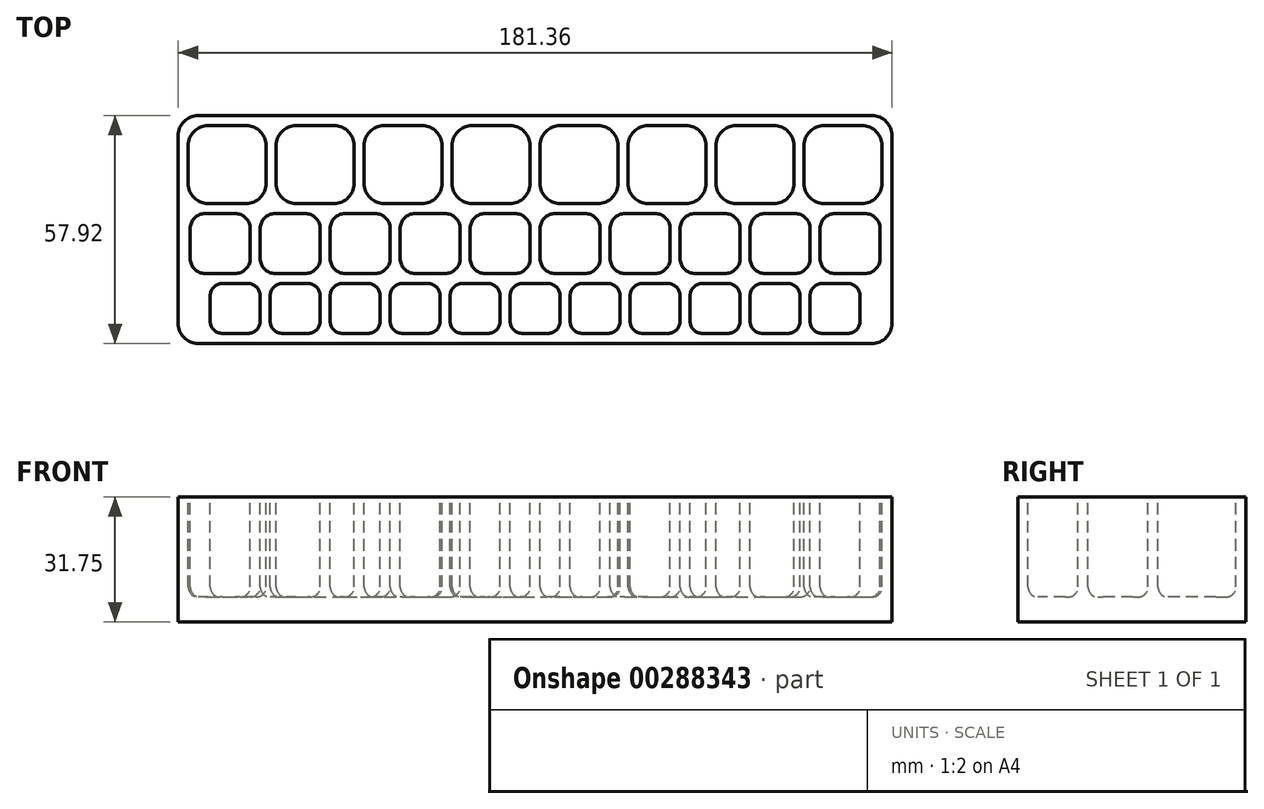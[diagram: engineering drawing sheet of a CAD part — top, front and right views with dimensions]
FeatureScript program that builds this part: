
annotation { "Feature Type Name" : "Feature", "Feature Type Description" : "" }
export const myFeature = defineFeature(function(context is Context, id is Id, definition is map)
    precondition{}
    {
        {
            var Q0;
            Q0=qCreatedBy(makeId("Top.planeOp"),FACE);
            var sketch = newSketch(context, id + "F0", { "sketchPlane" : qUnion([Q0])});
            skLineSegment(sketch, "E0.bottom", {"start": v(-90.68, 28.96) * mm, "end": v(90.68, 28.96) * mm});
            skLineSegment(sketch, "E0.top", {"start": v(-90.68, -28.96) * mm, "end": v(90.68, -28.96) * mm});
            skLineSegment(sketch, "E0.left", {"start": v(-90.68, 28.96) * mm, "end": v(-90.68, -28.96) * mm});
            skLineSegment(sketch, "E0.right", {"start": v(90.68, 28.96) * mm, "end": v(90.68, -28.96) * mm});
            skLineSegment(sketch, "E1.bottom", {"start": v(-88.14, 26.42) * mm, "end": v(-68.33, 26.42) * mm});
            skLineSegment(sketch, "E1.top", {"start": v(-88.14, 6.6) * mm, "end": v(-68.33, 6.6) * mm});
            skLineSegment(sketch, "E1.left", {"start": v(-88.14, 26.42) * mm, "end": v(-88.14, 6.6) * mm});
            skLineSegment(sketch, "E1.right", {"start": v(-68.33, 26.42) * mm, "end": v(-68.33, 6.6) * mm});
            skLineSegment(sketch, "E2.1.0.0", {"start": v(-65.79, 6.6) * mm, "end": v(-45.97, 6.6) * mm});
            skLineSegment(sketch, "E2.1.0.1", {"start": v(-45.97, 26.42) * mm, "end": v(-45.97, 6.6) * mm});
            skLineSegment(sketch, "E2.1.0.2", {"start": v(-65.79, 26.42) * mm, "end": v(-45.97, 26.42) * mm});
            skLineSegment(sketch, "E2.1.0.3", {"start": v(-65.79, 26.42) * mm, "end": v(-65.79, 6.6) * mm});
            skLineSegment(sketch, "E2.2.0.0", {"start": v(-43.43, 6.6) * mm, "end": v(-23.62, 6.6) * mm});
            skLineSegment(sketch, "E2.2.0.1", {"start": v(-23.62, 26.42) * mm, "end": v(-23.62, 6.6) * mm});
            skLineSegment(sketch, "E2.2.0.2", {"start": v(-43.43, 26.42) * mm, "end": v(-23.62, 26.42) * mm});
            skLineSegment(sketch, "E2.2.0.3", {"start": v(-43.43, 26.42) * mm, "end": v(-43.43, 6.6) * mm});
            skLineSegment(sketch, "E2.direction1", {"start": v(-88.14, 6.6) * mm, "end": v(-65.79, 6.6) * mm, "construction": true});
            skLineSegment(sketch, "E3.0.3.0", {"start": v(-21.08, 6.6) * mm, "end": v(-1.27, 6.6) * mm});
            skLineSegment(sketch, "E3.3.3.0", {"start": v(-1.27, 26.42) * mm, "end": v(-1.27, 6.6) * mm});
            skLineSegment(sketch, "E3.6.3.0", {"start": v(-21.08, 26.42) * mm, "end": v(-1.27, 26.42) * mm});
            skLineSegment(sketch, "E3.9.3.0", {"start": v(-21.08, 26.42) * mm, "end": v(-21.08, 6.6) * mm});
            skLineSegment(sketch, "E3.0.4.0", {"start": v(1.27, 6.6) * mm, "end": v(21.08, 6.6) * mm});
            skLineSegment(sketch, "E3.3.4.0", {"start": v(21.08, 26.42) * mm, "end": v(21.08, 6.6) * mm});
            skLineSegment(sketch, "E3.6.4.0", {"start": v(1.27, 26.42) * mm, "end": v(21.08, 26.42) * mm});
            skLineSegment(sketch, "E3.9.4.0", {"start": v(1.27, 26.42) * mm, "end": v(1.27, 6.6) * mm});
            skLineSegment(sketch, "E3.0.5.0", {"start": v(23.62, 6.6) * mm, "end": v(43.43, 6.6) * mm});
            skLineSegment(sketch, "E3.3.5.0", {"start": v(43.43, 26.42) * mm, "end": v(43.43, 6.6) * mm});
            skLineSegment(sketch, "E3.6.5.0", {"start": v(23.62, 26.42) * mm, "end": v(43.43, 26.42) * mm});
            skLineSegment(sketch, "E3.9.5.0", {"start": v(23.62, 26.42) * mm, "end": v(23.62, 6.6) * mm});
            skLineSegment(sketch, "E3.0.6.0", {"start": v(45.97, 6.6) * mm, "end": v(65.79, 6.6) * mm});
            skLineSegment(sketch, "E3.3.6.0", {"start": v(65.79, 26.42) * mm, "end": v(65.79, 6.6) * mm});
            skLineSegment(sketch, "E3.6.6.0", {"start": v(45.97, 26.42) * mm, "end": v(65.79, 26.42) * mm});
            skLineSegment(sketch, "E3.9.6.0", {"start": v(45.97, 26.42) * mm, "end": v(45.97, 6.6) * mm});
            skLineSegment(sketch, "E3.0.7.0", {"start": v(68.33, 6.6) * mm, "end": v(88.14, 6.6) * mm});
            skLineSegment(sketch, "E3.3.7.0", {"start": v(88.14, 26.42) * mm, "end": v(88.14, 6.6) * mm});
            skLineSegment(sketch, "E3.6.7.0", {"start": v(68.33, 26.42) * mm, "end": v(88.14, 26.42) * mm});
            skLineSegment(sketch, "E3.9.7.0", {"start": v(68.33, 26.42) * mm, "end": v(68.33, 6.6) * mm});
            skLineSegment(sketch, "E4.bottom", {"start": v(-87.63, 4.06) * mm, "end": v(-72.4, 4.06) * mm});
            skLineSegment(sketch, "E4.top", {"start": v(-87.63, -11.18) * mm, "end": v(-72.4, -11.18) * mm});
            skLineSegment(sketch, "E4.left", {"start": v(-87.63, 4.06) * mm, "end": v(-87.63, -11.18) * mm});
            skLineSegment(sketch, "E4.right", {"start": v(-72.4, 4.06) * mm, "end": v(-72.4, -11.18) * mm});
            skLineSegment(sketch, "E5.1.0.0", {"start": v(-54.61, 4.06) * mm, "end": v(-54.61, -11.18) * mm});
            skLineSegment(sketch, "E5.1.0.1", {"start": v(-69.85, 4.06) * mm, "end": v(-54.61, 4.06) * mm});
            skLineSegment(sketch, "E5.1.0.2", {"start": v(-69.85, 4.06) * mm, "end": v(-69.85, -11.18) * mm});
            skLineSegment(sketch, "E5.1.0.3", {"start": v(-69.85, -11.18) * mm, "end": v(-54.61, -11.18) * mm});
            skLineSegment(sketch, "E5.2.0.0", {"start": v(-36.83, 4.06) * mm, "end": v(-36.83, -11.18) * mm});
            skLineSegment(sketch, "E5.2.0.1", {"start": v(-52.07, 4.06) * mm, "end": v(-36.83, 4.06) * mm});
            skLineSegment(sketch, "E5.2.0.2", {"start": v(-52.07, 4.06) * mm, "end": v(-52.07, -11.18) * mm});
            skLineSegment(sketch, "E5.2.0.3", {"start": v(-52.07, -11.18) * mm, "end": v(-36.83, -11.18) * mm});
            skLineSegment(sketch, "E5.3.0.0", {"start": v(-19.05, 4.06) * mm, "end": v(-19.05, -11.18) * mm});
            skLineSegment(sketch, "E5.3.0.1", {"start": v(-34.3, 4.06) * mm, "end": v(-19.05, 4.06) * mm});
            skLineSegment(sketch, "E5.3.0.2", {"start": v(-34.29, 4.06) * mm, "end": v(-34.29, -11.18) * mm});
            skLineSegment(sketch, "E5.3.0.3", {"start": v(-34.3, -11.18) * mm, "end": v(-19.05, -11.18) * mm});
            skLineSegment(sketch, "E5.4.0.0", {"start": v(-1.27, 4.06) * mm, "end": v(-1.27, -11.18) * mm});
            skLineSegment(sketch, "E5.4.0.1", {"start": v(-16.5, 4.06) * mm, "end": v(-1.27, 4.06) * mm});
            skLineSegment(sketch, "E5.4.0.2", {"start": v(-16.5, 4.06) * mm, "end": v(-16.5, -11.18) * mm});
            skLineSegment(sketch, "E5.4.0.3", {"start": v(-16.5, -11.18) * mm, "end": v(-1.27, -11.18) * mm});
            skLineSegment(sketch, "E5.5.0.0", {"start": v(16.51, 4.06) * mm, "end": v(16.51, -11.18) * mm});
            skLineSegment(sketch, "E5.5.0.1", {"start": v(1.27, 4.06) * mm, "end": v(16.51, 4.06) * mm});
            skLineSegment(sketch, "E5.5.0.2", {"start": v(1.27, 4.06) * mm, "end": v(1.27, -11.18) * mm});
            skLineSegment(sketch, "E5.5.0.3", {"start": v(1.27, -11.18) * mm, "end": v(16.51, -11.18) * mm});
            skLineSegment(sketch, "E5.6.0.0", {"start": v(34.3, 4.06) * mm, "end": v(34.3, -11.18) * mm});
            skLineSegment(sketch, "E5.6.0.1", {"start": v(19.05, 4.06) * mm, "end": v(34.3, 4.06) * mm});
            skLineSegment(sketch, "E5.6.0.2", {"start": v(19.05, 4.06) * mm, "end": v(19.05, -11.18) * mm});
            skLineSegment(sketch, "E5.6.0.3", {"start": v(19.05, -11.18) * mm, "end": v(34.3, -11.18) * mm});
            skLineSegment(sketch, "E5.7.0.0", {"start": v(52.07, 4.06) * mm, "end": v(52.07, -11.18) * mm});
            skLineSegment(sketch, "E5.7.0.1", {"start": v(36.83, 4.06) * mm, "end": v(52.07, 4.06) * mm});
            skLineSegment(sketch, "E5.7.0.2", {"start": v(36.83, 4.06) * mm, "end": v(36.83, -11.18) * mm});
            skLineSegment(sketch, "E5.7.0.3", {"start": v(36.83, -11.18) * mm, "end": v(52.07, -11.18) * mm});
            skLineSegment(sketch, "E5.direction1", {"start": v(-72.4, -11.18) * mm, "end": v(-54.61, -11.18) * mm, "construction": true});
            skLineSegment(sketch, "E6.bottom", {"start": v(-82.55, -13.72) * mm, "end": v(-69.85, -13.72) * mm});
            skLineSegment(sketch, "E6.top", {"start": v(-82.55, -26.42) * mm, "end": v(-69.85, -26.42) * mm});
            skLineSegment(sketch, "E6.left", {"start": v(-82.55, -13.72) * mm, "end": v(-82.55, -26.42) * mm});
            skLineSegment(sketch, "E6.right", {"start": v(-69.85, -13.72) * mm, "end": v(-69.85, -26.42) * mm});
            skLineSegment(sketch, "E7.1.0.0", {"start": v(-67.31, -13.72) * mm, "end": v(-54.61, -13.72) * mm});
            skLineSegment(sketch, "E7.1.0.1", {"start": v(-67.31, -13.72) * mm, "end": v(-67.31, -26.42) * mm});
            skLineSegment(sketch, "E7.1.0.2", {"start": v(-67.31, -26.42) * mm, "end": v(-54.61, -26.42) * mm});
            skLineSegment(sketch, "E7.1.0.3", {"start": v(-54.61, -13.72) * mm, "end": v(-54.61, -26.42) * mm});
            skLineSegment(sketch, "E7.2.0.0", {"start": v(-52.07, -13.72) * mm, "end": v(-39.37, -13.72) * mm});
            skLineSegment(sketch, "E7.2.0.1", {"start": v(-52.07, -13.72) * mm, "end": v(-52.07, -26.42) * mm});
            skLineSegment(sketch, "E7.2.0.2", {"start": v(-52.07, -26.42) * mm, "end": v(-39.37, -26.42) * mm});
            skLineSegment(sketch, "E7.2.0.3", {"start": v(-39.37, -13.72) * mm, "end": v(-39.37, -26.42) * mm});
            skLineSegment(sketch, "E7.3.0.0", {"start": v(-36.83, -13.72) * mm, "end": v(-24.13, -13.72) * mm});
            skLineSegment(sketch, "E7.3.0.1", {"start": v(-36.83, -13.72) * mm, "end": v(-36.83, -26.42) * mm});
            skLineSegment(sketch, "E7.3.0.2", {"start": v(-36.83, -26.42) * mm, "end": v(-24.13, -26.42) * mm});
            skLineSegment(sketch, "E7.3.0.3", {"start": v(-24.13, -13.72) * mm, "end": v(-24.13, -26.42) * mm});
            skLineSegment(sketch, "E7.4.0.0", {"start": v(-21.59, -13.72) * mm, "end": v(-8.89, -13.72) * mm});
            skLineSegment(sketch, "E7.4.0.1", {"start": v(-21.59, -13.72) * mm, "end": v(-21.59, -26.42) * mm});
            skLineSegment(sketch, "E7.4.0.2", {"start": v(-21.59, -26.42) * mm, "end": v(-8.89, -26.42) * mm});
            skLineSegment(sketch, "E7.4.0.3", {"start": v(-8.89, -13.72) * mm, "end": v(-8.89, -26.42) * mm});
            skLineSegment(sketch, "E7.5.0.0", {"start": v(-6.35, -13.72) * mm, "end": v(6.35, -13.72) * mm});
            skLineSegment(sketch, "E7.5.0.1", {"start": v(-6.35, -13.72) * mm, "end": v(-6.35, -26.42) * mm});
            skLineSegment(sketch, "E7.5.0.2", {"start": v(-6.35, -26.42) * mm, "end": v(6.35, -26.42) * mm});
            skLineSegment(sketch, "E7.5.0.3", {"start": v(6.35, -13.72) * mm, "end": v(6.35, -26.42) * mm});
            skLineSegment(sketch, "E7.6.0.0", {"start": v(8.9, -13.72) * mm, "end": v(21.6, -13.72) * mm});
            skLineSegment(sketch, "E7.6.0.1", {"start": v(8.9, -13.72) * mm, "end": v(8.9, -26.42) * mm});
            skLineSegment(sketch, "E7.6.0.2", {"start": v(8.9, -26.42) * mm, "end": v(21.6, -26.42) * mm});
            skLineSegment(sketch, "E7.6.0.3", {"start": v(21.6, -13.72) * mm, "end": v(21.6, -26.42) * mm});
            skLineSegment(sketch, "E7.7.0.0", {"start": v(24.13, -13.72) * mm, "end": v(36.83, -13.72) * mm});
            skLineSegment(sketch, "E7.7.0.1", {"start": v(24.13, -13.72) * mm, "end": v(24.13, -26.42) * mm});
            skLineSegment(sketch, "E7.7.0.2", {"start": v(24.13, -26.42) * mm, "end": v(36.83, -26.42) * mm});
            skLineSegment(sketch, "E7.7.0.3", {"start": v(36.83, -13.72) * mm, "end": v(36.83, -26.42) * mm});
            skLineSegment(sketch, "E7.direction1", {"start": v(-82.55, -26.42) * mm, "end": v(-67.31, -26.42) * mm, "construction": true});
            skLineSegment(sketch, "E8", {"start": v(-88.14, 26.42) * mm, "end": v(-88.14, 28.96) * mm, "construction": true});
            skLineSegment(sketch, "E9.0.8.0", {"start": v(69.85, 4.06) * mm, "end": v(69.85, -11.18) * mm});
            skLineSegment(sketch, "E9.3.8.0", {"start": v(54.61, 4.06) * mm, "end": v(69.85, 4.06) * mm});
            skLineSegment(sketch, "E9.6.8.0", {"start": v(54.61, 4.06) * mm, "end": v(54.61, -11.18) * mm});
            skLineSegment(sketch, "E9.9.8.0", {"start": v(54.61, -11.18) * mm, "end": v(69.85, -11.18) * mm});
            skLineSegment(sketch, "E9.0.9.0", {"start": v(87.63, 4.06) * mm, "end": v(87.63, -11.18) * mm});
            skLineSegment(sketch, "E9.3.9.0", {"start": v(72.4, 4.06) * mm, "end": v(87.63, 4.06) * mm});
            skLineSegment(sketch, "E9.6.9.0", {"start": v(72.4, 4.06) * mm, "end": v(72.4, -11.18) * mm});
            skLineSegment(sketch, "E9.9.9.0", {"start": v(72.4, -11.18) * mm, "end": v(87.63, -11.18) * mm});
            skLineSegment(sketch, "E10.0.8.0", {"start": v(39.37, -13.72) * mm, "end": v(52.07, -13.72) * mm});
            skLineSegment(sketch, "E10.3.8.0", {"start": v(39.37, -13.72) * mm, "end": v(39.37, -26.42) * mm});
            skLineSegment(sketch, "E10.6.8.0", {"start": v(39.37, -26.42) * mm, "end": v(52.07, -26.42) * mm});
            skLineSegment(sketch, "E10.9.8.0", {"start": v(52.07, -13.72) * mm, "end": v(52.07, -26.42) * mm});
            skLineSegment(sketch, "E10.0.9.0", {"start": v(54.61, -13.72) * mm, "end": v(67.31, -13.72) * mm});
            skLineSegment(sketch, "E10.3.9.0", {"start": v(54.61, -13.72) * mm, "end": v(54.61, -26.42) * mm});
            skLineSegment(sketch, "E10.6.9.0", {"start": v(54.61, -26.42) * mm, "end": v(67.31, -26.42) * mm});
            skLineSegment(sketch, "E10.9.9.0", {"start": v(67.31, -13.72) * mm, "end": v(67.31, -26.42) * mm});
            skLineSegment(sketch, "E10.0.10.0", {"start": v(69.85, -13.72) * mm, "end": v(82.55, -13.72) * mm});
            skLineSegment(sketch, "E10.3.10.0", {"start": v(69.85, -13.72) * mm, "end": v(69.85, -26.42) * mm});
            skLineSegment(sketch, "E10.6.10.0", {"start": v(69.85, -26.42) * mm, "end": v(82.55, -26.42) * mm});
            skLineSegment(sketch, "E10.9.10.0", {"start": v(82.55, -13.72) * mm, "end": v(82.55, -26.42) * mm});
            skLineSegment(sketch, "E11", {"start": v(82.55, -20.07) * mm, "end": v(90.68, -20.07) * mm, "construction": true});
            skLineSegment(sketch, "E12", {"start": v(-87.63, -3.56) * mm, "end": v(-90.68, -3.56) * mm, "construction": true});
            skLineSegment(sketch, "E13", {"start": v(87.63, -3.56) * mm, "end": v(90.68, -3.56) * mm, "construction": true});
            skLineSegment(sketch, "E14", {"start": v(88.14, 16.5) * mm, "end": v(90.68, 16.5) * mm, "construction": true});
            skLineSegment(sketch, "E15", {"start": v(-88.14, 16.5) * mm, "end": v(-90.68, 16.5) * mm, "construction": true});
            skLineSegment(sketch, "E16", {"start": v(-76.2, -26.42) * mm, "end": v(-76.2, -28.96) * mm, "construction": true});
            skLineSegment(sketch, "E17", {"start": v(-80.01, -11.18) * mm, "end": v(-80.01, -13.72) * mm, "construction": true});
            skLineSegment(sketch, "E18", {"start": v(-78.23, 6.6) * mm, "end": v(-78.23, 4.06) * mm, "construction": true});
            skLineSegment(sketch, "E19", {"start": v(-78.23, 26.42) * mm, "end": v(-78.23, 28.96) * mm, "construction": true});
            skLineSegment(sketch, "E20", {"start": v(-82.55, -20.07) * mm, "end": v(-90.68, -20.07) * mm, "construction": true});
            skLineSegment(sketch, "E21", {"start": v(-90.68, 0) * mm, "end": v(0, 0) * mm, "construction": true});
            skLineSegment(sketch, "E22", {"start": v(0, 0) * mm, "end": v(90.68, 0) * mm, "construction": true});
            skSolve(sketch);
        }
        {
            var Q0;
            Q0 = qSketchRegion(id + "F0", true);
            var Q1;
            Q1=makeQuery(id+"F0.imprint","IMPRINT",FACE,{"disambiguationData":[TD([[makeQuery(id+"F0.imprint","IMPRINT",EDGE,{"derivedFrom":sQuery(id+"F0.wireOp",EDGE,"E1.bottom")}),-1.0]])]});
            var Q2;
            Q2=makeQuery(id+"F0.imprint","IMPRINT",FACE,{"disambiguationData":[TD([[makeQuery(id+"F0.imprint","IMPRINT",EDGE,{"derivedFrom":sQuery(id+"F0.wireOp",EDGE,"E2.1.0.0")}),1.0]])]});
            var Q3;
            Q3=makeQuery(id+"F0.imprint","IMPRINT",FACE,{"disambiguationData":[TD([[makeQuery(id+"F0.imprint","IMPRINT",EDGE,{"derivedFrom":sQuery(id+"F0.wireOp",EDGE,"E2.2.0.0")}),1.0]])]});
            var Q4;
            Q4=makeQuery(id+"F0.imprint","IMPRINT",FACE,{"disambiguationData":[TD([[makeQuery(id+"F0.imprint","IMPRINT",EDGE,{"derivedFrom":sQuery(id+"F0.wireOp",EDGE,"E3.0.3.0")}),1.0]])]});
            var Q5;
            Q5=makeQuery(id+"F0.imprint","IMPRINT",FACE,{"disambiguationData":[TD([[makeQuery(id+"F0.imprint","IMPRINT",EDGE,{"derivedFrom":sQuery(id+"F0.wireOp",EDGE,"E3.0.4.0")}),1.0]])]});
            var Q6;
            Q6=makeQuery(id+"F0.imprint","IMPRINT",FACE,{"disambiguationData":[TD([[makeQuery(id+"F0.imprint","IMPRINT",EDGE,{"derivedFrom":sQuery(id+"F0.wireOp",EDGE,"E3.0.5.0")}),1.0]])]});
            var Q7;
            Q7=makeQuery(id+"F0.imprint","IMPRINT",FACE,{"disambiguationData":[TD([[makeQuery(id+"F0.imprint","IMPRINT",EDGE,{"derivedFrom":sQuery(id+"F0.wireOp",EDGE,"E3.0.6.0")}),1.0]])]});
            var Q8;
            Q8=makeQuery(id+"F0.imprint","IMPRINT",FACE,{"disambiguationData":[TD([[makeQuery(id+"F0.imprint","IMPRINT",EDGE,{"derivedFrom":sQuery(id+"F0.wireOp",EDGE,"E3.0.7.0")}),1.0]])]});
            var Q9;
            Q9=makeQuery(id+"F0.imprint","IMPRINT",FACE,{"disambiguationData":[TD([[makeQuery(id+"F0.imprint","IMPRINT",EDGE,{"derivedFrom":sQuery(id+"F0.wireOp",EDGE,"E4.bottom")}),-1.0]])]});
            var Q10;
            Q10=makeQuery(id+"F0.imprint","IMPRINT",FACE,{"disambiguationData":[TD([[makeQuery(id+"F0.imprint","IMPRINT",EDGE,{"derivedFrom":sQuery(id+"F0.wireOp",EDGE,"E5.1.0.0")}),-1.0]])]});
            var Q11;
            Q11=makeQuery(id+"F0.imprint","IMPRINT",FACE,{"disambiguationData":[TD([[makeQuery(id+"F0.imprint","IMPRINT",EDGE,{"derivedFrom":sQuery(id+"F0.wireOp",EDGE,"E5.2.0.0")}),-1.0]])]});
            var Q12;
            Q12=makeQuery(id+"F0.imprint","IMPRINT",FACE,{"disambiguationData":[TD([[makeQuery(id+"F0.imprint","IMPRINT",EDGE,{"derivedFrom":sQuery(id+"F0.wireOp",EDGE,"E5.3.0.0")}),-1.0]])]});
            var Q13;
            Q13=makeQuery(id+"F0.imprint","IMPRINT",FACE,{"disambiguationData":[TD([[makeQuery(id+"F0.imprint","IMPRINT",EDGE,{"derivedFrom":sQuery(id+"F0.wireOp",EDGE,"E5.4.0.0")}),-1.0]])]});
            var Q14;
            Q14=makeQuery(id+"F0.imprint","IMPRINT",FACE,{"disambiguationData":[TD([[makeQuery(id+"F0.imprint","IMPRINT",EDGE,{"derivedFrom":sQuery(id+"F0.wireOp",EDGE,"E5.5.0.0")}),-1.0]])]});
            var Q15;
            Q15=makeQuery(id+"F0.imprint","IMPRINT",FACE,{"disambiguationData":[TD([[makeQuery(id+"F0.imprint","IMPRINT",EDGE,{"derivedFrom":sQuery(id+"F0.wireOp",EDGE,"E5.6.0.0")}),-1.0]])]});
            var Q16;
            Q16=makeQuery(id+"F0.imprint","IMPRINT",FACE,{"disambiguationData":[TD([[makeQuery(id+"F0.imprint","IMPRINT",EDGE,{"derivedFrom":sQuery(id+"F0.wireOp",EDGE,"E5.7.0.0")}),-1.0]])]});
            var Q17;
            Q17=makeQuery(id+"F0.imprint","IMPRINT",FACE,{"disambiguationData":[TD([[makeQuery(id+"F0.imprint","IMPRINT",EDGE,{"derivedFrom":sQuery(id+"F0.wireOp",EDGE,"E9.0.8.0")}),-1.0]])]});
            var Q18;
            Q18=makeQuery(id+"F0.imprint","IMPRINT",FACE,{"disambiguationData":[TD([[makeQuery(id+"F0.imprint","IMPRINT",EDGE,{"derivedFrom":sQuery(id+"F0.wireOp",EDGE,"E9.0.9.0")}),-1.0]])]});
            var Q19;
            Q19=makeQuery(id+"F0.imprint","IMPRINT",FACE,{"disambiguationData":[TD([[makeQuery(id+"F0.imprint","IMPRINT",EDGE,{"derivedFrom":sQuery(id+"F0.wireOp",EDGE,"E6.bottom")}),-1.0]])]});
            var Q20;
            Q20=makeQuery(id+"F0.imprint","IMPRINT",FACE,{"disambiguationData":[TD([[makeQuery(id+"F0.imprint","IMPRINT",EDGE,{"derivedFrom":sQuery(id+"F0.wireOp",EDGE,"E7.1.0.0")}),-1.0]])]});
            var Q21;
            Q21=makeQuery(id+"F0.imprint","IMPRINT",FACE,{"disambiguationData":[TD([[makeQuery(id+"F0.imprint","IMPRINT",EDGE,{"derivedFrom":sQuery(id+"F0.wireOp",EDGE,"E7.2.0.0")}),-1.0]])]});
            var Q22;
            Q22=makeQuery(id+"F0.imprint","IMPRINT",FACE,{"disambiguationData":[TD([[makeQuery(id+"F0.imprint","IMPRINT",EDGE,{"derivedFrom":sQuery(id+"F0.wireOp",EDGE,"E7.3.0.0")}),-1.0]])]});
            var Q23;
            Q23=makeQuery(id+"F0.imprint","IMPRINT",FACE,{"disambiguationData":[TD([[makeQuery(id+"F0.imprint","IMPRINT",EDGE,{"derivedFrom":sQuery(id+"F0.wireOp",EDGE,"E7.4.0.0")}),-1.0]])]});
            var Q24;
            Q24=makeQuery(id+"F0.imprint","IMPRINT",FACE,{"disambiguationData":[TD([[makeQuery(id+"F0.imprint","IMPRINT",EDGE,{"derivedFrom":sQuery(id+"F0.wireOp",EDGE,"E7.5.0.0")}),-1.0]])]});
            var Q25;
            Q25=makeQuery(id+"F0.imprint","IMPRINT",FACE,{"disambiguationData":[TD([[makeQuery(id+"F0.imprint","IMPRINT",EDGE,{"derivedFrom":sQuery(id+"F0.wireOp",EDGE,"E7.6.0.0")}),-1.0]])]});
            var Q26;
            Q26=makeQuery(id+"F0.imprint","IMPRINT",FACE,{"disambiguationData":[TD([[makeQuery(id+"F0.imprint","IMPRINT",EDGE,{"derivedFrom":sQuery(id+"F0.wireOp",EDGE,"E7.7.0.0")}),-1.0]])]});
            var Q27;
            Q27=makeQuery(id+"F0.imprint","IMPRINT",FACE,{"disambiguationData":[TD([[makeQuery(id+"F0.imprint","IMPRINT",EDGE,{"derivedFrom":sQuery(id+"F0.wireOp",EDGE,"E10.0.8.0")}),-1.0]])]});
            var Q28;
            Q28=makeQuery(id+"F0.imprint","IMPRINT",FACE,{"disambiguationData":[TD([[makeQuery(id+"F0.imprint","IMPRINT",EDGE,{"derivedFrom":sQuery(id+"F0.wireOp",EDGE,"E10.0.9.0")}),-1.0]])]});
            var Q29;
            Q29=makeQuery(id+"F0.imprint","IMPRINT",FACE,{"disambiguationData":[TD([[makeQuery(id+"F0.imprint","IMPRINT",EDGE,{"derivedFrom":sQuery(id+"F0.wireOp",EDGE,"E10.0.10.0")}),-1.0]])]});
            extrude(context, id + "F1", {"entities" : qUnion([Q0, Q1, Q2, Q3, Q4, Q5, Q6, Q7, Q8, Q9, Q10, Q11, Q12, Q13, Q14, Q15, Q16, Q17, Q18, Q19, Q20, Q21, Q22, Q23, Q24, Q25, Q26, Q27, Q28, Q29]), "oppositeDirection" : true, "depth" : 31.75 * mm});
        }
        {
            var Q0;
            Q0=makeQuery(id+"F0.imprint","IMPRINT",FACE,{"disambiguationData":[TD([[makeQuery(id+"F0.imprint","IMPRINT",EDGE,{"derivedFrom":sQuery(id+"F0.wireOp",EDGE,"E6.bottom")}),-1.0]])]});
            var Q1;
            Q1=makeQuery(id+"F0.imprint","IMPRINT",FACE,{"disambiguationData":[TD([[makeQuery(id+"F0.imprint","IMPRINT",EDGE,{"derivedFrom":sQuery(id+"F0.wireOp",EDGE,"E7.1.0.0")}),-1.0]])]});
            var Q2;
            Q2=makeQuery(id+"F0.imprint","IMPRINT",FACE,{"disambiguationData":[TD([[makeQuery(id+"F0.imprint","IMPRINT",EDGE,{"derivedFrom":sQuery(id+"F0.wireOp",EDGE,"E4.bottom")}),-1.0]])]});
            var Q3;
            Q3=makeQuery(id+"F0.imprint","IMPRINT",FACE,{"disambiguationData":[TD([[makeQuery(id+"F0.imprint","IMPRINT",EDGE,{"derivedFrom":sQuery(id+"F0.wireOp",EDGE,"E5.1.0.0")}),-1.0]])]});
            var Q4;
            Q4=makeQuery(id+"F0.imprint","IMPRINT",FACE,{"disambiguationData":[TD([[makeQuery(id+"F0.imprint","IMPRINT",EDGE,{"derivedFrom":sQuery(id+"F0.wireOp",EDGE,"E5.2.0.0")}),-1.0]])]});
            var Q5;
            Q5=makeQuery(id+"F0.imprint","IMPRINT",FACE,{"disambiguationData":[TD([[makeQuery(id+"F0.imprint","IMPRINT",EDGE,{"derivedFrom":sQuery(id+"F0.wireOp",EDGE,"E7.2.0.0")}),-1.0]])]});
            var Q6;
            Q6=makeQuery(id+"F0.imprint","IMPRINT",FACE,{"disambiguationData":[TD([[makeQuery(id+"F0.imprint","IMPRINT",EDGE,{"derivedFrom":sQuery(id+"F0.wireOp",EDGE,"E7.3.0.0")}),-1.0]])]});
            var Q7;
            Q7=makeQuery(id+"F0.imprint","IMPRINT",FACE,{"disambiguationData":[TD([[makeQuery(id+"F0.imprint","IMPRINT",EDGE,{"derivedFrom":sQuery(id+"F0.wireOp",EDGE,"E7.4.0.0")}),-1.0]])]});
            var Q8;
            Q8=makeQuery(id+"F0.imprint","IMPRINT",FACE,{"disambiguationData":[TD([[makeQuery(id+"F0.imprint","IMPRINT",EDGE,{"derivedFrom":sQuery(id+"F0.wireOp",EDGE,"E5.3.0.0")}),-1.0]])]});
            var Q9;
            Q9=makeQuery(id+"F0.imprint","IMPRINT",FACE,{"disambiguationData":[TD([[makeQuery(id+"F0.imprint","IMPRINT",EDGE,{"derivedFrom":sQuery(id+"F0.wireOp",EDGE,"E5.4.0.0")}),-1.0]])]});
            var Q10;
            Q10=makeQuery(id+"F0.imprint","IMPRINT",FACE,{"disambiguationData":[TD([[makeQuery(id+"F0.imprint","IMPRINT",EDGE,{"derivedFrom":sQuery(id+"F0.wireOp",EDGE,"E7.5.0.0")}),-1.0]])]});
            var Q11;
            Q11=makeQuery(id+"F0.imprint","IMPRINT",FACE,{"disambiguationData":[TD([[makeQuery(id+"F0.imprint","IMPRINT",EDGE,{"derivedFrom":sQuery(id+"F0.wireOp",EDGE,"E7.6.0.0")}),-1.0]])]});
            var Q12;
            Q12=makeQuery(id+"F0.imprint","IMPRINT",FACE,{"disambiguationData":[TD([[makeQuery(id+"F0.imprint","IMPRINT",EDGE,{"derivedFrom":sQuery(id+"F0.wireOp",EDGE,"E5.5.0.0")}),-1.0]])]});
            var Q13;
            Q13=makeQuery(id+"F0.imprint","IMPRINT",FACE,{"disambiguationData":[TD([[makeQuery(id+"F0.imprint","IMPRINT",EDGE,{"derivedFrom":sQuery(id+"F0.wireOp",EDGE,"E5.6.0.0")}),-1.0]])]});
            var Q14;
            Q14=makeQuery(id+"F0.imprint","IMPRINT",FACE,{"disambiguationData":[TD([[makeQuery(id+"F0.imprint","IMPRINT",EDGE,{"derivedFrom":sQuery(id+"F0.wireOp",EDGE,"E7.7.0.0")}),-1.0]])]});
            var Q15;
            Q15=makeQuery(id+"F0.imprint","IMPRINT",FACE,{"disambiguationData":[TD([[makeQuery(id+"F0.imprint","IMPRINT",EDGE,{"derivedFrom":sQuery(id+"F0.wireOp",EDGE,"E10.0.8.0")}),-1.0]])]});
            var Q16;
            Q16=makeQuery(id+"F0.imprint","IMPRINT",FACE,{"disambiguationData":[TD([[makeQuery(id+"F0.imprint","IMPRINT",EDGE,{"derivedFrom":sQuery(id+"F0.wireOp",EDGE,"E5.7.0.0")}),-1.0]])]});
            var Q17;
            Q17=makeQuery(id+"F0.imprint","IMPRINT",FACE,{"disambiguationData":[TD([[makeQuery(id+"F0.imprint","IMPRINT",EDGE,{"derivedFrom":sQuery(id+"F0.wireOp",EDGE,"E9.0.8.0")}),-1.0]])]});
            var Q18;
            Q18=makeQuery(id+"F0.imprint","IMPRINT",FACE,{"disambiguationData":[TD([[makeQuery(id+"F0.imprint","IMPRINT",EDGE,{"derivedFrom":sQuery(id+"F0.wireOp",EDGE,"E10.0.9.0")}),-1.0]])]});
            var Q19;
            Q19=makeQuery(id+"F0.imprint","IMPRINT",FACE,{"disambiguationData":[TD([[makeQuery(id+"F0.imprint","IMPRINT",EDGE,{"derivedFrom":sQuery(id+"F0.wireOp",EDGE,"E10.0.10.0")}),-1.0]])]});
            var Q20;
            Q20=makeQuery(id+"F0.imprint","IMPRINT",FACE,{"disambiguationData":[TD([[makeQuery(id+"F0.imprint","IMPRINT",EDGE,{"derivedFrom":sQuery(id+"F0.wireOp",EDGE,"E9.0.9.0")}),-1.0]])]});
            var Q21;
            Q21=makeQuery(id+"F0.imprint","IMPRINT",FACE,{"disambiguationData":[TD([[makeQuery(id+"F0.imprint","IMPRINT",EDGE,{"derivedFrom":sQuery(id+"F0.wireOp",EDGE,"E3.0.7.0")}),1.0]])]});
            var Q22;
            Q22=makeQuery(id+"F0.imprint","IMPRINT",FACE,{"disambiguationData":[TD([[makeQuery(id+"F0.imprint","IMPRINT",EDGE,{"derivedFrom":sQuery(id+"F0.wireOp",EDGE,"E3.0.6.0")}),1.0]])]});
            var Q23;
            Q23=makeQuery(id+"F0.imprint","IMPRINT",FACE,{"disambiguationData":[TD([[makeQuery(id+"F0.imprint","IMPRINT",EDGE,{"derivedFrom":sQuery(id+"F0.wireOp",EDGE,"E3.0.5.0")}),1.0]])]});
            var Q24;
            Q24=makeQuery(id+"F0.imprint","IMPRINT",FACE,{"disambiguationData":[TD([[makeQuery(id+"F0.imprint","IMPRINT",EDGE,{"derivedFrom":sQuery(id+"F0.wireOp",EDGE,"E3.0.4.0")}),1.0]])]});
            var Q25;
            Q25=makeQuery(id+"F0.imprint","IMPRINT",FACE,{"disambiguationData":[TD([[makeQuery(id+"F0.imprint","IMPRINT",EDGE,{"derivedFrom":sQuery(id+"F0.wireOp",EDGE,"E3.0.3.0")}),1.0]])]});
            var Q26;
            Q26=makeQuery(id+"F0.imprint","IMPRINT",FACE,{"disambiguationData":[TD([[makeQuery(id+"F0.imprint","IMPRINT",EDGE,{"derivedFrom":sQuery(id+"F0.wireOp",EDGE,"E2.2.0.0")}),1.0]])]});
            var Q27;
            Q27=makeQuery(id+"F0.imprint","IMPRINT",FACE,{"disambiguationData":[TD([[makeQuery(id+"F0.imprint","IMPRINT",EDGE,{"derivedFrom":sQuery(id+"F0.wireOp",EDGE,"E2.1.0.0")}),1.0]])]});
            var Q28;
            Q28=makeQuery(id+"F0.imprint","IMPRINT",FACE,{"disambiguationData":[TD([[makeQuery(id+"F0.imprint","IMPRINT",EDGE,{"derivedFrom":sQuery(id+"F0.wireOp",EDGE,"E1.bottom")}),-1.0]])]});
            extrude(context, id + "F2", {"entities" : qUnion([Q0, Q1, Q2, Q3, Q4, Q5, Q6, Q7, Q8, Q9, Q10, Q11, Q12, Q13, Q14, Q15, Q16, Q17, Q18, Q19, Q20, Q21, Q22, Q23, Q24, Q25, Q26, Q27, Q28]), "operationType" : NewBodyOperationType.REMOVE, "oppositeDirection" : true, "depth" : 25.4 * mm});
        }
        {
            var Q0;
            Q0=makeQuery(id+"F2.boolean.opBoolean","COPY",EDGE,{"derivedFrom":makeQuery(id+"F2.opExtrude","SWEPT_EDGE",EDGE,{"disambiguationData":[OSD([sQuery(id+"F0.wireOp",EDGE,"E3.6.3.0"),sQuery(id+"F0.wireOp",EDGE,"E3.9.3.0")])]})});
            var Q1;
            Q1=makeQuery(id+"F2.boolean.opBoolean","COPY",EDGE,{"derivedFrom":makeQuery(id+"F2.opExtrude","SWEPT_EDGE",EDGE,{"disambiguationData":[OSD([sQuery(id+"F0.wireOp",EDGE,"E2.2.0.2"),sQuery(id+"F0.wireOp",EDGE,"E2.2.0.3")])]})});
            var Q2;
            Q2=makeQuery(id+"F2.boolean.opBoolean","COPY",EDGE,{"derivedFrom":makeQuery(id+"F2.opExtrude","SWEPT_EDGE",EDGE,{"disambiguationData":[OSD([sQuery(id+"F0.wireOp",EDGE,"E2.1.0.2"),sQuery(id+"F0.wireOp",EDGE,"E2.1.0.3")])]})});
            var Q3;
            Q3=makeQuery(id+"F2.boolean.opBoolean","COPY",EDGE,{"derivedFrom":makeQuery(id+"F2.opExtrude","SWEPT_EDGE",EDGE,{"disambiguationData":[OSD([sQuery(id+"F0.wireOp",EDGE,"E1.bottom"),sQuery(id+"F0.wireOp",EDGE,"E1.left")])]})});
            var Q4;
            Q4=makeQuery(id+"F2.boolean.opBoolean","COPY",EDGE,{"derivedFrom":makeQuery(id+"F2.opExtrude","SWEPT_EDGE",EDGE,{"disambiguationData":[OSD([sQuery(id+"F0.wireOp",EDGE,"E3.6.4.0"),sQuery(id+"F0.wireOp",EDGE,"E3.9.4.0")])]})});
            var Q5;
            Q5=makeQuery(id+"F2.boolean.opBoolean","COPY",EDGE,{"derivedFrom":makeQuery(id+"F2.opExtrude","SWEPT_EDGE",EDGE,{"disambiguationData":[OSD([sQuery(id+"F0.wireOp",EDGE,"E3.6.5.0"),sQuery(id+"F0.wireOp",EDGE,"E3.9.5.0")])]})});
            var Q6;
            Q6=makeQuery(id+"F2.boolean.opBoolean","COPY",EDGE,{"derivedFrom":makeQuery(id+"F2.opExtrude","SWEPT_EDGE",EDGE,{"disambiguationData":[OSD([sQuery(id+"F0.wireOp",EDGE,"E3.6.6.0"),sQuery(id+"F0.wireOp",EDGE,"E3.9.6.0")])]})});
            var Q7;
            Q7=makeQuery(id+"F2.boolean.opBoolean","COPY",EDGE,{"derivedFrom":makeQuery(id+"F2.opExtrude","SWEPT_EDGE",EDGE,{"disambiguationData":[OSD([sQuery(id+"F0.wireOp",EDGE,"E3.6.7.0"),sQuery(id+"F0.wireOp",EDGE,"E3.9.7.0")])]})});
            var Q8;
            Q8=makeQuery(id+"F2.boolean.opBoolean","COPY",EDGE,{"derivedFrom":makeQuery(id+"F2.opExtrude","SWEPT_EDGE",EDGE,{"disambiguationData":[OSD([sQuery(id+"F0.wireOp",EDGE,"E3.3.7.0"),sQuery(id+"F0.wireOp",EDGE,"E3.6.7.0")])]})});
            var Q9;
            Q9=makeQuery(id+"F2.boolean.opBoolean","COPY",EDGE,{"derivedFrom":makeQuery(id+"F2.opExtrude","SWEPT_EDGE",EDGE,{"disambiguationData":[OSD([sQuery(id+"F0.wireOp",EDGE,"E3.3.6.0"),sQuery(id+"F0.wireOp",EDGE,"E3.6.6.0")])]})});
            var Q10;
            Q10=makeQuery(id+"F2.boolean.opBoolean","COPY",EDGE,{"derivedFrom":makeQuery(id+"F2.opExtrude","SWEPT_EDGE",EDGE,{"disambiguationData":[OSD([sQuery(id+"F0.wireOp",EDGE,"E3.3.5.0"),sQuery(id+"F0.wireOp",EDGE,"E3.6.5.0")])]})});
            var Q11;
            Q11=makeQuery(id+"F2.boolean.opBoolean","COPY",EDGE,{"derivedFrom":makeQuery(id+"F2.opExtrude","SWEPT_EDGE",EDGE,{"disambiguationData":[OSD([sQuery(id+"F0.wireOp",EDGE,"E3.3.4.0"),sQuery(id+"F0.wireOp",EDGE,"E3.6.4.0")])]})});
            var Q12;
            Q12=makeQuery(id+"F2.boolean.opBoolean","COPY",EDGE,{"derivedFrom":makeQuery(id+"F2.opExtrude","SWEPT_EDGE",EDGE,{"disambiguationData":[OSD([sQuery(id+"F0.wireOp",EDGE,"E3.3.3.0"),sQuery(id+"F0.wireOp",EDGE,"E3.6.3.0")])]})});
            var Q13;
            Q13=makeQuery(id+"F2.boolean.opBoolean","COPY",EDGE,{"derivedFrom":makeQuery(id+"F2.opExtrude","SWEPT_EDGE",EDGE,{"disambiguationData":[OSD([sQuery(id+"F0.wireOp",EDGE,"E2.2.0.1"),sQuery(id+"F0.wireOp",EDGE,"E2.2.0.2")])]})});
            var Q14;
            Q14=makeQuery(id+"F2.boolean.opBoolean","COPY",EDGE,{"derivedFrom":makeQuery(id+"F2.opExtrude","SWEPT_EDGE",EDGE,{"disambiguationData":[OSD([sQuery(id+"F0.wireOp",EDGE,"E1.bottom"),sQuery(id+"F0.wireOp",EDGE,"E1.right")])]})});
            var Q15;
            Q15=makeQuery(id+"F2.boolean.opBoolean","COPY",EDGE,{"derivedFrom":makeQuery(id+"F2.opExtrude","SWEPT_EDGE",EDGE,{"disambiguationData":[OSD([sQuery(id+"F0.wireOp",EDGE,"E1.top"),sQuery(id+"F0.wireOp",EDGE,"E1.right")])]})});
            var Q16;
            Q16=makeQuery(id+"F2.boolean.opBoolean","COPY",EDGE,{"derivedFrom":makeQuery(id+"F2.opExtrude","SWEPT_EDGE",EDGE,{"disambiguationData":[OSD([sQuery(id+"F0.wireOp",EDGE,"E2.1.0.0"),sQuery(id+"F0.wireOp",EDGE,"E2.1.0.1")])]})});
            var Q17;
            Q17=makeQuery(id+"F2.boolean.opBoolean","COPY",EDGE,{"derivedFrom":makeQuery(id+"F2.opExtrude","SWEPT_EDGE",EDGE,{"disambiguationData":[OSD([sQuery(id+"F0.wireOp",EDGE,"E2.2.0.0"),sQuery(id+"F0.wireOp",EDGE,"E2.2.0.1")])]})});
            var Q18;
            Q18=makeQuery(id+"F2.boolean.opBoolean","COPY",EDGE,{"derivedFrom":makeQuery(id+"F2.opExtrude","SWEPT_EDGE",EDGE,{"disambiguationData":[OSD([sQuery(id+"F0.wireOp",EDGE,"E3.0.3.0"),sQuery(id+"F0.wireOp",EDGE,"E3.3.3.0")])]})});
            var Q19;
            Q19=makeQuery(id+"F2.boolean.opBoolean","COPY",EDGE,{"derivedFrom":makeQuery(id+"F2.opExtrude","SWEPT_EDGE",EDGE,{"disambiguationData":[OSD([sQuery(id+"F0.wireOp",EDGE,"E3.0.4.0"),sQuery(id+"F0.wireOp",EDGE,"E3.3.4.0")])]})});
            var Q20;
            Q20=makeQuery(id+"F2.boolean.opBoolean","COPY",EDGE,{"derivedFrom":makeQuery(id+"F2.opExtrude","SWEPT_EDGE",EDGE,{"disambiguationData":[OSD([sQuery(id+"F0.wireOp",EDGE,"E3.0.5.0"),sQuery(id+"F0.wireOp",EDGE,"E3.3.5.0")])]})});
            var Q21;
            Q21=makeQuery(id+"F2.boolean.opBoolean","COPY",EDGE,{"derivedFrom":makeQuery(id+"F2.opExtrude","SWEPT_EDGE",EDGE,{"disambiguationData":[OSD([sQuery(id+"F0.wireOp",EDGE,"E3.0.6.0"),sQuery(id+"F0.wireOp",EDGE,"E3.3.6.0")])]})});
            var Q22;
            Q22=makeQuery(id+"F2.boolean.opBoolean","COPY",EDGE,{"derivedFrom":makeQuery(id+"F2.opExtrude","SWEPT_EDGE",EDGE,{"disambiguationData":[OSD([sQuery(id+"F0.wireOp",EDGE,"E3.0.7.0"),sQuery(id+"F0.wireOp",EDGE,"E3.3.7.0")])]})});
            var Q23;
            Q23=makeQuery(id+"F2.boolean.opBoolean","COPY",EDGE,{"derivedFrom":makeQuery(id+"F2.opExtrude","SWEPT_EDGE",EDGE,{"disambiguationData":[OSD([sQuery(id+"F0.wireOp",EDGE,"E3.0.7.0"),sQuery(id+"F0.wireOp",EDGE,"E3.9.7.0")])]})});
            var Q24;
            Q24=makeQuery(id+"F2.boolean.opBoolean","COPY",EDGE,{"derivedFrom":makeQuery(id+"F2.opExtrude","SWEPT_EDGE",EDGE,{"disambiguationData":[OSD([sQuery(id+"F0.wireOp",EDGE,"E3.0.6.0"),sQuery(id+"F0.wireOp",EDGE,"E3.9.6.0")])]})});
            var Q25;
            Q25=makeQuery(id+"F2.boolean.opBoolean","COPY",EDGE,{"derivedFrom":makeQuery(id+"F2.opExtrude","SWEPT_EDGE",EDGE,{"disambiguationData":[OSD([sQuery(id+"F0.wireOp",EDGE,"E3.0.5.0"),sQuery(id+"F0.wireOp",EDGE,"E3.9.5.0")])]})});
            var Q26;
            Q26=makeQuery(id+"F2.boolean.opBoolean","COPY",EDGE,{"derivedFrom":makeQuery(id+"F2.opExtrude","SWEPT_EDGE",EDGE,{"disambiguationData":[OSD([sQuery(id+"F0.wireOp",EDGE,"E3.0.4.0"),sQuery(id+"F0.wireOp",EDGE,"E3.9.4.0")])]})});
            var Q27;
            Q27=makeQuery(id+"F2.boolean.opBoolean","COPY",EDGE,{"derivedFrom":makeQuery(id+"F2.opExtrude","SWEPT_EDGE",EDGE,{"disambiguationData":[OSD([sQuery(id+"F0.wireOp",EDGE,"E3.0.3.0"),sQuery(id+"F0.wireOp",EDGE,"E3.9.3.0")])]})});
            var Q28;
            Q28=makeQuery(id+"F2.boolean.opBoolean","COPY",EDGE,{"derivedFrom":makeQuery(id+"F2.opExtrude","SWEPT_EDGE",EDGE,{"disambiguationData":[OSD([sQuery(id+"F0.wireOp",EDGE,"E2.2.0.0"),sQuery(id+"F0.wireOp",EDGE,"E2.2.0.3")])]})});
            var Q29;
            Q29=makeQuery(id+"F2.boolean.opBoolean","COPY",EDGE,{"derivedFrom":makeQuery(id+"F2.opExtrude","SWEPT_EDGE",EDGE,{"disambiguationData":[OSD([sQuery(id+"F0.wireOp",EDGE,"E2.1.0.0"),sQuery(id+"F0.wireOp",EDGE,"E2.1.0.3")])]})});
            var Q30;
            Q30=makeQuery(id+"F2.boolean.opBoolean","COPY",EDGE,{"derivedFrom":makeQuery(id+"F2.opExtrude","SWEPT_EDGE",EDGE,{"disambiguationData":[OSD([sQuery(id+"F0.wireOp",EDGE,"E1.top"),sQuery(id+"F0.wireOp",EDGE,"E1.left")])]})});
            var Q31;
            Q31=makeQuery(id+"F2.boolean.opBoolean","COPY",EDGE,{"derivedFrom":makeQuery(id+"F2.opExtrude","SWEPT_EDGE",EDGE,{"disambiguationData":[OSD([sQuery(id+"F0.wireOp",EDGE,"E2.1.0.1"),sQuery(id+"F0.wireOp",EDGE,"E2.1.0.2")])]})});
            fillet(context, id + "F3", {"entities" : qUnion([Q0, Q1, Q2, Q3, Q4, Q5, Q6, Q7, Q8, Q9, Q10, Q11, Q12, Q13, Q14, Q15, Q16, Q17, Q18, Q19, Q20, Q21, Q22, Q23, Q24, Q25, Q26, Q27, Q28, Q29, Q30, Q31]), "radius" : 5.08 * mm, "tangentPropagation" : true, "allowEdgeOverflow" : false});
        }
        {
            var Q0;
            Q0=makeQuery(id+"F2.boolean.opBoolean","COPY",EDGE,{"derivedFrom":makeQuery(id+"F2.opExtrude","SWEPT_EDGE",EDGE,{"disambiguationData":[OSD([sQuery(id+"F0.wireOp",EDGE,"E4.bottom"),sQuery(id+"F0.wireOp",EDGE,"E4.right")])]})});
            var Q1;
            Q1=makeQuery(id+"F2.boolean.opBoolean","COPY",EDGE,{"derivedFrom":makeQuery(id+"F2.opExtrude","SWEPT_EDGE",EDGE,{"disambiguationData":[OSD([sQuery(id+"F0.wireOp",EDGE,"E5.1.0.0"),sQuery(id+"F0.wireOp",EDGE,"E5.1.0.1")])]})});
            var Q2;
            Q2=makeQuery(id+"F2.boolean.opBoolean","COPY",EDGE,{"derivedFrom":makeQuery(id+"F2.opExtrude","SWEPT_EDGE",EDGE,{"disambiguationData":[OSD([sQuery(id+"F0.wireOp",EDGE,"E5.2.0.0"),sQuery(id+"F0.wireOp",EDGE,"E5.2.0.1")])]})});
            var Q3;
            Q3=makeQuery(id+"F2.boolean.opBoolean","COPY",EDGE,{"derivedFrom":makeQuery(id+"F2.opExtrude","SWEPT_EDGE",EDGE,{"disambiguationData":[OSD([sQuery(id+"F0.wireOp",EDGE,"E5.3.0.0"),sQuery(id+"F0.wireOp",EDGE,"E5.3.0.1")])]})});
            var Q4;
            Q4=makeQuery(id+"F2.boolean.opBoolean","COPY",EDGE,{"derivedFrom":makeQuery(id+"F2.opExtrude","SWEPT_EDGE",EDGE,{"disambiguationData":[OSD([sQuery(id+"F0.wireOp",EDGE,"E5.4.0.0"),sQuery(id+"F0.wireOp",EDGE,"E5.4.0.1")])]})});
            var Q5;
            Q5=makeQuery(id+"F2.boolean.opBoolean","COPY",EDGE,{"derivedFrom":makeQuery(id+"F2.opExtrude","SWEPT_EDGE",EDGE,{"disambiguationData":[OSD([sQuery(id+"F0.wireOp",EDGE,"E5.5.0.0"),sQuery(id+"F0.wireOp",EDGE,"E5.5.0.1")])]})});
            var Q6;
            Q6=makeQuery(id+"F2.boolean.opBoolean","COPY",EDGE,{"derivedFrom":makeQuery(id+"F2.opExtrude","SWEPT_EDGE",EDGE,{"disambiguationData":[OSD([sQuery(id+"F0.wireOp",EDGE,"E5.6.0.0"),sQuery(id+"F0.wireOp",EDGE,"E5.6.0.1")])]})});
            var Q7;
            Q7=makeQuery(id+"F2.boolean.opBoolean","COPY",EDGE,{"derivedFrom":makeQuery(id+"F2.opExtrude","SWEPT_EDGE",EDGE,{"disambiguationData":[OSD([sQuery(id+"F0.wireOp",EDGE,"E5.7.0.0"),sQuery(id+"F0.wireOp",EDGE,"E5.7.0.1")])]})});
            var Q8;
            Q8=makeQuery(id+"F2.boolean.opBoolean","COPY",EDGE,{"derivedFrom":makeQuery(id+"F2.opExtrude","SWEPT_EDGE",EDGE,{"disambiguationData":[OSD([sQuery(id+"F0.wireOp",EDGE,"E9.0.8.0"),sQuery(id+"F0.wireOp",EDGE,"E9.3.8.0")])]})});
            var Q9;
            Q9=makeQuery(id+"F2.boolean.opBoolean","COPY",EDGE,{"derivedFrom":makeQuery(id+"F2.opExtrude","SWEPT_EDGE",EDGE,{"disambiguationData":[OSD([sQuery(id+"F0.wireOp",EDGE,"E9.0.9.0"),sQuery(id+"F0.wireOp",EDGE,"E9.3.9.0")])]})});
            var Q10;
            Q10=makeQuery(id+"F2.boolean.opBoolean","COPY",EDGE,{"derivedFrom":makeQuery(id+"F2.opExtrude","SWEPT_EDGE",EDGE,{"disambiguationData":[OSD([sQuery(id+"F0.wireOp",EDGE,"E4.top"),sQuery(id+"F0.wireOp",EDGE,"E4.right")])]})});
            var Q11;
            Q11=makeQuery(id+"F2.boolean.opBoolean","COPY",EDGE,{"derivedFrom":makeQuery(id+"F2.opExtrude","SWEPT_EDGE",EDGE,{"disambiguationData":[OSD([sQuery(id+"F0.wireOp",EDGE,"E5.1.0.0"),sQuery(id+"F0.wireOp",EDGE,"E5.1.0.3")])]})});
            var Q12;
            Q12=makeQuery(id+"F2.boolean.opBoolean","COPY",EDGE,{"derivedFrom":makeQuery(id+"F2.opExtrude","SWEPT_EDGE",EDGE,{"disambiguationData":[OSD([sQuery(id+"F0.wireOp",EDGE,"E5.2.0.0"),sQuery(id+"F0.wireOp",EDGE,"E5.2.0.3")])]})});
            var Q13;
            Q13=makeQuery(id+"F2.boolean.opBoolean","COPY",EDGE,{"derivedFrom":makeQuery(id+"F2.opExtrude","SWEPT_EDGE",EDGE,{"disambiguationData":[OSD([sQuery(id+"F0.wireOp",EDGE,"E5.3.0.0"),sQuery(id+"F0.wireOp",EDGE,"E5.3.0.3")])]})});
            var Q14;
            Q14=makeQuery(id+"F2.boolean.opBoolean","COPY",EDGE,{"derivedFrom":makeQuery(id+"F2.opExtrude","SWEPT_EDGE",EDGE,{"disambiguationData":[OSD([sQuery(id+"F0.wireOp",EDGE,"E5.4.0.0"),sQuery(id+"F0.wireOp",EDGE,"E5.4.0.3")])]})});
            var Q15;
            Q15=makeQuery(id+"F2.boolean.opBoolean","COPY",EDGE,{"derivedFrom":makeQuery(id+"F2.opExtrude","SWEPT_EDGE",EDGE,{"disambiguationData":[OSD([sQuery(id+"F0.wireOp",EDGE,"E5.5.0.0"),sQuery(id+"F0.wireOp",EDGE,"E5.5.0.3")])]})});
            var Q16;
            Q16=makeQuery(id+"F2.boolean.opBoolean","COPY",EDGE,{"derivedFrom":makeQuery(id+"F2.opExtrude","SWEPT_EDGE",EDGE,{"disambiguationData":[OSD([sQuery(id+"F0.wireOp",EDGE,"E5.6.0.0"),sQuery(id+"F0.wireOp",EDGE,"E5.6.0.3")])]})});
            var Q17;
            Q17=makeQuery(id+"F2.boolean.opBoolean","COPY",EDGE,{"derivedFrom":makeQuery(id+"F2.opExtrude","SWEPT_EDGE",EDGE,{"disambiguationData":[OSD([sQuery(id+"F0.wireOp",EDGE,"E5.7.0.0"),sQuery(id+"F0.wireOp",EDGE,"E5.7.0.3")])]})});
            var Q18;
            Q18=makeQuery(id+"F2.boolean.opBoolean","COPY",EDGE,{"derivedFrom":makeQuery(id+"F2.opExtrude","SWEPT_EDGE",EDGE,{"disambiguationData":[OSD([sQuery(id+"F0.wireOp",EDGE,"E9.0.8.0"),sQuery(id+"F0.wireOp",EDGE,"E9.9.8.0")])]})});
            var Q19;
            Q19=makeQuery(id+"F2.boolean.opBoolean","COPY",EDGE,{"derivedFrom":makeQuery(id+"F2.opExtrude","SWEPT_EDGE",EDGE,{"disambiguationData":[OSD([sQuery(id+"F0.wireOp",EDGE,"E9.0.9.0"),sQuery(id+"F0.wireOp",EDGE,"E9.9.9.0")])]})});
            var Q20;
            Q20=makeQuery(id+"F2.boolean.opBoolean","COPY",EDGE,{"derivedFrom":makeQuery(id+"F2.opExtrude","SWEPT_EDGE",EDGE,{"disambiguationData":[OSD([sQuery(id+"F0.wireOp",EDGE,"E9.6.9.0"),sQuery(id+"F0.wireOp",EDGE,"E9.9.9.0")])]})});
            var Q21;
            Q21=makeQuery(id+"F2.boolean.opBoolean","COPY",EDGE,{"derivedFrom":makeQuery(id+"F2.opExtrude","SWEPT_EDGE",EDGE,{"disambiguationData":[OSD([sQuery(id+"F0.wireOp",EDGE,"E9.6.8.0"),sQuery(id+"F0.wireOp",EDGE,"E9.9.8.0")])]})});
            var Q22;
            Q22=makeQuery(id+"F2.boolean.opBoolean","COPY",EDGE,{"derivedFrom":makeQuery(id+"F2.opExtrude","SWEPT_EDGE",EDGE,{"disambiguationData":[OSD([sQuery(id+"F0.wireOp",EDGE,"E5.7.0.2"),sQuery(id+"F0.wireOp",EDGE,"E5.7.0.3")])]})});
            var Q23;
            Q23=makeQuery(id+"F2.boolean.opBoolean","COPY",EDGE,{"derivedFrom":makeQuery(id+"F2.opExtrude","SWEPT_EDGE",EDGE,{"disambiguationData":[OSD([sQuery(id+"F0.wireOp",EDGE,"E5.6.0.2"),sQuery(id+"F0.wireOp",EDGE,"E5.6.0.3")])]})});
            var Q24;
            Q24=makeQuery(id+"F2.boolean.opBoolean","COPY",EDGE,{"derivedFrom":makeQuery(id+"F2.opExtrude","SWEPT_EDGE",EDGE,{"disambiguationData":[OSD([sQuery(id+"F0.wireOp",EDGE,"E5.5.0.2"),sQuery(id+"F0.wireOp",EDGE,"E5.5.0.3")])]})});
            var Q25;
            Q25=makeQuery(id+"F2.boolean.opBoolean","COPY",EDGE,{"derivedFrom":makeQuery(id+"F2.opExtrude","SWEPT_EDGE",EDGE,{"disambiguationData":[OSD([sQuery(id+"F0.wireOp",EDGE,"E5.4.0.2"),sQuery(id+"F0.wireOp",EDGE,"E5.4.0.3")])]})});
            var Q26;
            Q26=makeQuery(id+"F2.boolean.opBoolean","COPY",EDGE,{"derivedFrom":makeQuery(id+"F2.opExtrude","SWEPT_EDGE",EDGE,{"disambiguationData":[OSD([sQuery(id+"F0.wireOp",EDGE,"E5.3.0.2"),sQuery(id+"F0.wireOp",EDGE,"E5.3.0.3")])]})});
            var Q27;
            Q27=makeQuery(id+"F2.boolean.opBoolean","COPY",EDGE,{"derivedFrom":makeQuery(id+"F2.opExtrude","SWEPT_EDGE",EDGE,{"disambiguationData":[OSD([sQuery(id+"F0.wireOp",EDGE,"E5.2.0.2"),sQuery(id+"F0.wireOp",EDGE,"E5.2.0.3")])]})});
            var Q28;
            Q28=makeQuery(id+"F2.boolean.opBoolean","COPY",EDGE,{"derivedFrom":makeQuery(id+"F2.opExtrude","SWEPT_EDGE",EDGE,{"disambiguationData":[OSD([sQuery(id+"F0.wireOp",EDGE,"E5.1.0.2"),sQuery(id+"F0.wireOp",EDGE,"E5.1.0.3")])]})});
            var Q29;
            Q29=makeQuery(id+"F2.boolean.opBoolean","COPY",EDGE,{"derivedFrom":makeQuery(id+"F2.opExtrude","SWEPT_EDGE",EDGE,{"disambiguationData":[OSD([sQuery(id+"F0.wireOp",EDGE,"E4.top"),sQuery(id+"F0.wireOp",EDGE,"E4.left")])]})});
            var Q30;
            Q30=makeQuery(id+"F2.boolean.opBoolean","COPY",EDGE,{"derivedFrom":makeQuery(id+"F2.opExtrude","SWEPT_EDGE",EDGE,{"disambiguationData":[OSD([sQuery(id+"F0.wireOp",EDGE,"E4.bottom"),sQuery(id+"F0.wireOp",EDGE,"E4.left")])]})});
            var Q31;
            Q31=makeQuery(id+"F2.boolean.opBoolean","COPY",EDGE,{"derivedFrom":makeQuery(id+"F2.opExtrude","SWEPT_EDGE",EDGE,{"disambiguationData":[OSD([sQuery(id+"F0.wireOp",EDGE,"E5.1.0.1"),sQuery(id+"F0.wireOp",EDGE,"E5.1.0.2")])]})});
            var Q32;
            Q32=makeQuery(id+"F2.boolean.opBoolean","COPY",EDGE,{"derivedFrom":makeQuery(id+"F2.opExtrude","SWEPT_EDGE",EDGE,{"disambiguationData":[OSD([sQuery(id+"F0.wireOp",EDGE,"E5.2.0.1"),sQuery(id+"F0.wireOp",EDGE,"E5.2.0.2")])]})});
            var Q33;
            Q33=makeQuery(id+"F2.boolean.opBoolean","COPY",EDGE,{"derivedFrom":makeQuery(id+"F2.opExtrude","SWEPT_EDGE",EDGE,{"disambiguationData":[OSD([sQuery(id+"F0.wireOp",EDGE,"E5.3.0.1"),sQuery(id+"F0.wireOp",EDGE,"E5.3.0.2")])]})});
            var Q34;
            Q34=makeQuery(id+"F2.boolean.opBoolean","COPY",EDGE,{"derivedFrom":makeQuery(id+"F2.opExtrude","SWEPT_EDGE",EDGE,{"disambiguationData":[OSD([sQuery(id+"F0.wireOp",EDGE,"E5.4.0.1"),sQuery(id+"F0.wireOp",EDGE,"E5.4.0.2")])]})});
            var Q35;
            Q35=makeQuery(id+"F2.boolean.opBoolean","COPY",EDGE,{"derivedFrom":makeQuery(id+"F2.opExtrude","SWEPT_EDGE",EDGE,{"disambiguationData":[OSD([sQuery(id+"F0.wireOp",EDGE,"E5.5.0.1"),sQuery(id+"F0.wireOp",EDGE,"E5.5.0.2")])]})});
            var Q36;
            Q36=makeQuery(id+"F2.boolean.opBoolean","COPY",EDGE,{"derivedFrom":makeQuery(id+"F2.opExtrude","SWEPT_EDGE",EDGE,{"disambiguationData":[OSD([sQuery(id+"F0.wireOp",EDGE,"E5.6.0.1"),sQuery(id+"F0.wireOp",EDGE,"E5.6.0.2")])]})});
            var Q37;
            Q37=makeQuery(id+"F2.boolean.opBoolean","COPY",EDGE,{"derivedFrom":makeQuery(id+"F2.opExtrude","SWEPT_EDGE",EDGE,{"disambiguationData":[OSD([sQuery(id+"F0.wireOp",EDGE,"E5.7.0.1"),sQuery(id+"F0.wireOp",EDGE,"E5.7.0.2")])]})});
            var Q38;
            Q38=makeQuery(id+"F2.boolean.opBoolean","COPY",EDGE,{"derivedFrom":makeQuery(id+"F2.opExtrude","SWEPT_EDGE",EDGE,{"disambiguationData":[OSD([sQuery(id+"F0.wireOp",EDGE,"E9.3.8.0"),sQuery(id+"F0.wireOp",EDGE,"E9.6.8.0")])]})});
            var Q39;
            Q39=makeQuery(id+"F2.boolean.opBoolean","COPY",EDGE,{"derivedFrom":makeQuery(id+"F2.opExtrude","SWEPT_EDGE",EDGE,{"disambiguationData":[OSD([sQuery(id+"F0.wireOp",EDGE,"E9.3.9.0"),sQuery(id+"F0.wireOp",EDGE,"E9.6.9.0")])]})});
            fillet(context, id + "F4", {"entities" : qUnion([Q0, Q1, Q2, Q3, Q4, Q5, Q6, Q7, Q8, Q9, Q10, Q11, Q12, Q13, Q14, Q15, Q16, Q17, Q18, Q19, Q20, Q21, Q22, Q23, Q24, Q25, Q26, Q27, Q28, Q29, Q30, Q31, Q32, Q33, Q34, Q35, Q36, Q37, Q38, Q39]), "radius" : 3.8 * mm, "tangentPropagation" : true, "allowEdgeOverflow" : false});
        }
        {
            var Q0;
            Q0=makeQuery(id+"F2.boolean.opBoolean","COPY",EDGE,{"derivedFrom":makeQuery(id+"F2.opExtrude","SWEPT_EDGE",EDGE,{"disambiguationData":[OSD([sQuery(id+"F0.wireOp",EDGE,"E6.bottom"),sQuery(id+"F0.wireOp",EDGE,"E6.right")])]})});
            var Q1;
            Q1=makeQuery(id+"F2.boolean.opBoolean","COPY",EDGE,{"derivedFrom":makeQuery(id+"F2.opExtrude","SWEPT_EDGE",EDGE,{"disambiguationData":[OSD([sQuery(id+"F0.wireOp",EDGE,"E7.1.0.0"),sQuery(id+"F0.wireOp",EDGE,"E7.1.0.3")])]})});
            var Q2;
            Q2=makeQuery(id+"F2.boolean.opBoolean","COPY",EDGE,{"derivedFrom":makeQuery(id+"F2.opExtrude","SWEPT_EDGE",EDGE,{"disambiguationData":[OSD([sQuery(id+"F0.wireOp",EDGE,"E7.2.0.0"),sQuery(id+"F0.wireOp",EDGE,"E7.2.0.3")])]})});
            var Q3;
            Q3=makeQuery(id+"F2.boolean.opBoolean","COPY",EDGE,{"derivedFrom":makeQuery(id+"F2.opExtrude","SWEPT_EDGE",EDGE,{"disambiguationData":[OSD([sQuery(id+"F0.wireOp",EDGE,"E7.3.0.0"),sQuery(id+"F0.wireOp",EDGE,"E7.3.0.3")])]})});
            var Q4;
            Q4=makeQuery(id+"F2.boolean.opBoolean","COPY",EDGE,{"derivedFrom":makeQuery(id+"F2.opExtrude","SWEPT_EDGE",EDGE,{"disambiguationData":[OSD([sQuery(id+"F0.wireOp",EDGE,"E7.4.0.0"),sQuery(id+"F0.wireOp",EDGE,"E7.4.0.3")])]})});
            var Q5;
            Q5=makeQuery(id+"F2.boolean.opBoolean","COPY",EDGE,{"derivedFrom":makeQuery(id+"F2.opExtrude","SWEPT_EDGE",EDGE,{"disambiguationData":[OSD([sQuery(id+"F0.wireOp",EDGE,"E7.5.0.0"),sQuery(id+"F0.wireOp",EDGE,"E7.5.0.3")])]})});
            var Q6;
            Q6=makeQuery(id+"F2.boolean.opBoolean","COPY",EDGE,{"derivedFrom":makeQuery(id+"F2.opExtrude","SWEPT_EDGE",EDGE,{"disambiguationData":[OSD([sQuery(id+"F0.wireOp",EDGE,"E7.6.0.0"),sQuery(id+"F0.wireOp",EDGE,"E7.6.0.3")])]})});
            var Q7;
            Q7=makeQuery(id+"F2.boolean.opBoolean","COPY",EDGE,{"derivedFrom":makeQuery(id+"F2.opExtrude","SWEPT_EDGE",EDGE,{"disambiguationData":[OSD([sQuery(id+"F0.wireOp",EDGE,"E7.7.0.0"),sQuery(id+"F0.wireOp",EDGE,"E7.7.0.3")])]})});
            var Q8;
            Q8=makeQuery(id+"F2.boolean.opBoolean","COPY",EDGE,{"derivedFrom":makeQuery(id+"F2.opExtrude","SWEPT_EDGE",EDGE,{"disambiguationData":[OSD([sQuery(id+"F0.wireOp",EDGE,"E10.0.8.0"),sQuery(id+"F0.wireOp",EDGE,"E10.9.8.0")])]})});
            var Q9;
            Q9=makeQuery(id+"F2.boolean.opBoolean","COPY",EDGE,{"derivedFrom":makeQuery(id+"F2.opExtrude","SWEPT_EDGE",EDGE,{"disambiguationData":[OSD([sQuery(id+"F0.wireOp",EDGE,"E10.0.9.0"),sQuery(id+"F0.wireOp",EDGE,"E10.9.9.0")])]})});
            var Q10;
            Q10=makeQuery(id+"F2.boolean.opBoolean","COPY",EDGE,{"derivedFrom":makeQuery(id+"F2.opExtrude","SWEPT_EDGE",EDGE,{"disambiguationData":[OSD([sQuery(id+"F0.wireOp",EDGE,"E10.0.10.0"),sQuery(id+"F0.wireOp",EDGE,"E10.9.10.0")])]})});
            var Q11;
            Q11=makeQuery(id+"F2.boolean.opBoolean","COPY",EDGE,{"derivedFrom":makeQuery(id+"F2.opExtrude","SWEPT_EDGE",EDGE,{"disambiguationData":[OSD([sQuery(id+"F0.wireOp",EDGE,"E10.6.10.0"),sQuery(id+"F0.wireOp",EDGE,"E10.9.10.0")])]})});
            var Q12;
            Q12=makeQuery(id+"F2.boolean.opBoolean","COPY",EDGE,{"derivedFrom":makeQuery(id+"F2.opExtrude","SWEPT_EDGE",EDGE,{"disambiguationData":[OSD([sQuery(id+"F0.wireOp",EDGE,"E10.6.9.0"),sQuery(id+"F0.wireOp",EDGE,"E10.9.9.0")])]})});
            var Q13;
            Q13=makeQuery(id+"F2.boolean.opBoolean","COPY",EDGE,{"derivedFrom":makeQuery(id+"F2.opExtrude","SWEPT_EDGE",EDGE,{"disambiguationData":[OSD([sQuery(id+"F0.wireOp",EDGE,"E10.6.8.0"),sQuery(id+"F0.wireOp",EDGE,"E10.9.8.0")])]})});
            var Q14;
            Q14=makeQuery(id+"F2.boolean.opBoolean","COPY",EDGE,{"derivedFrom":makeQuery(id+"F2.opExtrude","SWEPT_EDGE",EDGE,{"disambiguationData":[OSD([sQuery(id+"F0.wireOp",EDGE,"E7.7.0.2"),sQuery(id+"F0.wireOp",EDGE,"E7.7.0.3")])]})});
            var Q15;
            Q15=makeQuery(id+"F2.boolean.opBoolean","COPY",EDGE,{"derivedFrom":makeQuery(id+"F2.opExtrude","SWEPT_EDGE",EDGE,{"disambiguationData":[OSD([sQuery(id+"F0.wireOp",EDGE,"E7.6.0.2"),sQuery(id+"F0.wireOp",EDGE,"E7.6.0.3")])]})});
            var Q16;
            Q16=makeQuery(id+"F2.boolean.opBoolean","COPY",EDGE,{"derivedFrom":makeQuery(id+"F2.opExtrude","SWEPT_EDGE",EDGE,{"disambiguationData":[OSD([sQuery(id+"F0.wireOp",EDGE,"E7.5.0.2"),sQuery(id+"F0.wireOp",EDGE,"E7.5.0.3")])]})});
            var Q17;
            Q17=makeQuery(id+"F2.boolean.opBoolean","COPY",EDGE,{"derivedFrom":makeQuery(id+"F2.opExtrude","SWEPT_EDGE",EDGE,{"disambiguationData":[OSD([sQuery(id+"F0.wireOp",EDGE,"E7.4.0.2"),sQuery(id+"F0.wireOp",EDGE,"E7.4.0.3")])]})});
            var Q18;
            Q18=makeQuery(id+"F2.boolean.opBoolean","COPY",EDGE,{"derivedFrom":makeQuery(id+"F2.opExtrude","SWEPT_EDGE",EDGE,{"disambiguationData":[OSD([sQuery(id+"F0.wireOp",EDGE,"E7.3.0.2"),sQuery(id+"F0.wireOp",EDGE,"E7.3.0.3")])]})});
            var Q19;
            Q19=makeQuery(id+"F2.boolean.opBoolean","COPY",EDGE,{"derivedFrom":makeQuery(id+"F2.opExtrude","SWEPT_EDGE",EDGE,{"disambiguationData":[OSD([sQuery(id+"F0.wireOp",EDGE,"E7.2.0.2"),sQuery(id+"F0.wireOp",EDGE,"E7.2.0.3")])]})});
            var Q20;
            Q20=makeQuery(id+"F2.boolean.opBoolean","COPY",EDGE,{"derivedFrom":makeQuery(id+"F2.opExtrude","SWEPT_EDGE",EDGE,{"disambiguationData":[OSD([sQuery(id+"F0.wireOp",EDGE,"E7.1.0.2"),sQuery(id+"F0.wireOp",EDGE,"E7.1.0.3")])]})});
            var Q21;
            Q21=makeQuery(id+"F2.boolean.opBoolean","COPY",EDGE,{"derivedFrom":makeQuery(id+"F2.opExtrude","SWEPT_EDGE",EDGE,{"disambiguationData":[OSD([sQuery(id+"F0.wireOp",EDGE,"E6.top"),sQuery(id+"F0.wireOp",EDGE,"E6.right")])]})});
            var Q22;
            Q22=makeQuery(id+"F2.boolean.opBoolean","COPY",EDGE,{"derivedFrom":makeQuery(id+"F2.opExtrude","SWEPT_EDGE",EDGE,{"disambiguationData":[OSD([sQuery(id+"F0.wireOp",EDGE,"E6.top"),sQuery(id+"F0.wireOp",EDGE,"E6.left")])]})});
            var Q23;
            Q23=makeQuery(id+"F2.boolean.opBoolean","COPY",EDGE,{"derivedFrom":makeQuery(id+"F2.opExtrude","SWEPT_EDGE",EDGE,{"disambiguationData":[OSD([sQuery(id+"F0.wireOp",EDGE,"E7.1.0.1"),sQuery(id+"F0.wireOp",EDGE,"E7.1.0.2")])]})});
            var Q24;
            Q24=makeQuery(id+"F2.boolean.opBoolean","COPY",EDGE,{"derivedFrom":makeQuery(id+"F2.opExtrude","SWEPT_EDGE",EDGE,{"disambiguationData":[OSD([sQuery(id+"F0.wireOp",EDGE,"E7.2.0.1"),sQuery(id+"F0.wireOp",EDGE,"E7.2.0.2")])]})});
            var Q25;
            Q25=makeQuery(id+"F2.boolean.opBoolean","COPY",EDGE,{"derivedFrom":makeQuery(id+"F2.opExtrude","SWEPT_EDGE",EDGE,{"disambiguationData":[OSD([sQuery(id+"F0.wireOp",EDGE,"E7.3.0.1"),sQuery(id+"F0.wireOp",EDGE,"E7.3.0.2")])]})});
            var Q26;
            Q26=makeQuery(id+"F2.boolean.opBoolean","COPY",EDGE,{"derivedFrom":makeQuery(id+"F2.opExtrude","SWEPT_EDGE",EDGE,{"disambiguationData":[OSD([sQuery(id+"F0.wireOp",EDGE,"E7.4.0.1"),sQuery(id+"F0.wireOp",EDGE,"E7.4.0.2")])]})});
            var Q27;
            Q27=makeQuery(id+"F2.boolean.opBoolean","COPY",EDGE,{"derivedFrom":makeQuery(id+"F2.opExtrude","SWEPT_EDGE",EDGE,{"disambiguationData":[OSD([sQuery(id+"F0.wireOp",EDGE,"E7.5.0.1"),sQuery(id+"F0.wireOp",EDGE,"E7.5.0.2")])]})});
            var Q28;
            Q28=makeQuery(id+"F2.boolean.opBoolean","COPY",EDGE,{"derivedFrom":makeQuery(id+"F2.opExtrude","SWEPT_EDGE",EDGE,{"disambiguationData":[OSD([sQuery(id+"F0.wireOp",EDGE,"E7.6.0.1"),sQuery(id+"F0.wireOp",EDGE,"E7.6.0.2")])]})});
            var Q29;
            Q29=makeQuery(id+"F2.boolean.opBoolean","COPY",EDGE,{"derivedFrom":makeQuery(id+"F2.opExtrude","SWEPT_EDGE",EDGE,{"disambiguationData":[OSD([sQuery(id+"F0.wireOp",EDGE,"E7.7.0.1"),sQuery(id+"F0.wireOp",EDGE,"E7.7.0.2")])]})});
            var Q30;
            Q30=makeQuery(id+"F2.boolean.opBoolean","COPY",EDGE,{"derivedFrom":makeQuery(id+"F2.opExtrude","SWEPT_EDGE",EDGE,{"disambiguationData":[OSD([sQuery(id+"F0.wireOp",EDGE,"E10.3.8.0"),sQuery(id+"F0.wireOp",EDGE,"E10.6.8.0")])]})});
            var Q31;
            Q31=makeQuery(id+"F2.boolean.opBoolean","COPY",EDGE,{"derivedFrom":makeQuery(id+"F2.opExtrude","SWEPT_EDGE",EDGE,{"disambiguationData":[OSD([sQuery(id+"F0.wireOp",EDGE,"E10.3.9.0"),sQuery(id+"F0.wireOp",EDGE,"E10.6.9.0")])]})});
            var Q32;
            Q32=makeQuery(id+"F2.boolean.opBoolean","COPY",EDGE,{"derivedFrom":makeQuery(id+"F2.opExtrude","SWEPT_EDGE",EDGE,{"disambiguationData":[OSD([sQuery(id+"F0.wireOp",EDGE,"E10.3.10.0"),sQuery(id+"F0.wireOp",EDGE,"E10.6.10.0")])]})});
            var Q33;
            Q33=makeQuery(id+"F2.boolean.opBoolean","COPY",EDGE,{"derivedFrom":makeQuery(id+"F2.opExtrude","SWEPT_EDGE",EDGE,{"disambiguationData":[OSD([sQuery(id+"F0.wireOp",EDGE,"E10.0.10.0"),sQuery(id+"F0.wireOp",EDGE,"E10.3.10.0")])]})});
            var Q34;
            Q34=makeQuery(id+"F2.boolean.opBoolean","COPY",EDGE,{"derivedFrom":makeQuery(id+"F2.opExtrude","SWEPT_EDGE",EDGE,{"disambiguationData":[OSD([sQuery(id+"F0.wireOp",EDGE,"E10.0.9.0"),sQuery(id+"F0.wireOp",EDGE,"E10.3.9.0")])]})});
            var Q35;
            Q35=makeQuery(id+"F2.boolean.opBoolean","COPY",EDGE,{"derivedFrom":makeQuery(id+"F2.opExtrude","SWEPT_EDGE",EDGE,{"disambiguationData":[OSD([sQuery(id+"F0.wireOp",EDGE,"E10.0.8.0"),sQuery(id+"F0.wireOp",EDGE,"E10.3.8.0")])]})});
            var Q36;
            Q36=makeQuery(id+"F2.boolean.opBoolean","COPY",EDGE,{"derivedFrom":makeQuery(id+"F2.opExtrude","SWEPT_EDGE",EDGE,{"disambiguationData":[OSD([sQuery(id+"F0.wireOp",EDGE,"E7.7.0.0"),sQuery(id+"F0.wireOp",EDGE,"E7.7.0.1")])]})});
            var Q37;
            Q37=makeQuery(id+"F2.boolean.opBoolean","COPY",EDGE,{"derivedFrom":makeQuery(id+"F2.opExtrude","SWEPT_EDGE",EDGE,{"disambiguationData":[OSD([sQuery(id+"F0.wireOp",EDGE,"E7.6.0.0"),sQuery(id+"F0.wireOp",EDGE,"E7.6.0.1")])]})});
            var Q38;
            Q38=makeQuery(id+"F2.boolean.opBoolean","COPY",EDGE,{"derivedFrom":makeQuery(id+"F2.opExtrude","SWEPT_EDGE",EDGE,{"disambiguationData":[OSD([sQuery(id+"F0.wireOp",EDGE,"E7.5.0.0"),sQuery(id+"F0.wireOp",EDGE,"E7.5.0.1")])]})});
            var Q39;
            Q39=makeQuery(id+"F2.boolean.opBoolean","COPY",EDGE,{"derivedFrom":makeQuery(id+"F2.opExtrude","SWEPT_EDGE",EDGE,{"disambiguationData":[OSD([sQuery(id+"F0.wireOp",EDGE,"E7.4.0.0"),sQuery(id+"F0.wireOp",EDGE,"E7.4.0.1")])]})});
            var Q40;
            Q40=makeQuery(id+"F2.boolean.opBoolean","COPY",EDGE,{"derivedFrom":makeQuery(id+"F2.opExtrude","SWEPT_EDGE",EDGE,{"disambiguationData":[OSD([sQuery(id+"F0.wireOp",EDGE,"E7.3.0.0"),sQuery(id+"F0.wireOp",EDGE,"E7.3.0.1")])]})});
            var Q41;
            Q41=makeQuery(id+"F2.boolean.opBoolean","COPY",EDGE,{"derivedFrom":makeQuery(id+"F2.opExtrude","SWEPT_EDGE",EDGE,{"disambiguationData":[OSD([sQuery(id+"F0.wireOp",EDGE,"E7.2.0.0"),sQuery(id+"F0.wireOp",EDGE,"E7.2.0.1")])]})});
            var Q42;
            Q42=makeQuery(id+"F2.boolean.opBoolean","COPY",EDGE,{"derivedFrom":makeQuery(id+"F2.opExtrude","SWEPT_EDGE",EDGE,{"disambiguationData":[OSD([sQuery(id+"F0.wireOp",EDGE,"E7.1.0.0"),sQuery(id+"F0.wireOp",EDGE,"E7.1.0.1")])]})});
            var Q43;
            Q43=makeQuery(id+"F2.boolean.opBoolean","COPY",EDGE,{"derivedFrom":makeQuery(id+"F2.opExtrude","SWEPT_EDGE",EDGE,{"disambiguationData":[OSD([sQuery(id+"F0.wireOp",EDGE,"E6.bottom"),sQuery(id+"F0.wireOp",EDGE,"E6.left")])]})});
            fillet(context, id + "F5", {"entities" : qUnion([Q0, Q1, Q2, Q3, Q4, Q5, Q6, Q7, Q8, Q9, Q10, Q11, Q12, Q13, Q14, Q15, Q16, Q17, Q18, Q19, Q20, Q21, Q22, Q23, Q24, Q25, Q26, Q27, Q28, Q29, Q30, Q31, Q32, Q33, Q34, Q35, Q36, Q37, Q38, Q39, Q40, Q41, Q42, Q43]), "radius" : 3.17 * mm, "tangentPropagation" : true, "allowEdgeOverflow" : false});
        }
        {
            var Q0;
            Q0=makeQuery(id+"F2.boolean.opBoolean","COPY",FACE,{"derivedFrom":makeQuery(id+"F2.opExtrude","CAP_FACE",FACE,{"disambiguationData":[OSD([sQuery(id+"F0.wireOp",EDGE,"E1.bottom"),sQuery(id+"F0.wireOp",EDGE,"E1.top"),sQuery(id+"F0.wireOp",EDGE,"E1.left"),sQuery(id+"F0.wireOp",EDGE,"E1.right")])],"isStart":false})});
            var Q1;
            Q1=makeQuery(id+"F2.boolean.opBoolean","COPY",FACE,{"derivedFrom":makeQuery(id+"F2.opExtrude","CAP_FACE",FACE,{"disambiguationData":[OSD([sQuery(id+"F0.wireOp",EDGE,"E2.1.0.0"),sQuery(id+"F0.wireOp",EDGE,"E2.1.0.1"),sQuery(id+"F0.wireOp",EDGE,"E2.1.0.2"),sQuery(id+"F0.wireOp",EDGE,"E2.1.0.3")])],"isStart":false})});
            var Q2;
            Q2=makeQuery(id+"F2.boolean.opBoolean","COPY",FACE,{"derivedFrom":makeQuery(id+"F2.opExtrude","CAP_FACE",FACE,{"disambiguationData":[OSD([sQuery(id+"F0.wireOp",EDGE,"E2.2.0.0"),sQuery(id+"F0.wireOp",EDGE,"E2.2.0.1"),sQuery(id+"F0.wireOp",EDGE,"E2.2.0.2"),sQuery(id+"F0.wireOp",EDGE,"E2.2.0.3")])],"isStart":false})});
            var Q3;
            Q3=makeQuery(id+"F2.boolean.opBoolean","COPY",FACE,{"derivedFrom":makeQuery(id+"F2.opExtrude","CAP_FACE",FACE,{"disambiguationData":[OSD([sQuery(id+"F0.wireOp",EDGE,"E3.0.3.0"),sQuery(id+"F0.wireOp",EDGE,"E3.3.3.0"),sQuery(id+"F0.wireOp",EDGE,"E3.6.3.0"),sQuery(id+"F0.wireOp",EDGE,"E3.9.3.0")])],"isStart":false})});
            var Q4;
            Q4=makeQuery(id+"F2.boolean.opBoolean","COPY",FACE,{"derivedFrom":makeQuery(id+"F2.opExtrude","CAP_FACE",FACE,{"disambiguationData":[OSD([sQuery(id+"F0.wireOp",EDGE,"E3.0.4.0"),sQuery(id+"F0.wireOp",EDGE,"E3.3.4.0"),sQuery(id+"F0.wireOp",EDGE,"E3.6.4.0"),sQuery(id+"F0.wireOp",EDGE,"E3.9.4.0")])],"isStart":false})});
            var Q5;
            Q5=makeQuery(id+"F2.boolean.opBoolean","COPY",FACE,{"derivedFrom":makeQuery(id+"F2.opExtrude","CAP_FACE",FACE,{"disambiguationData":[OSD([sQuery(id+"F0.wireOp",EDGE,"E3.0.5.0"),sQuery(id+"F0.wireOp",EDGE,"E3.3.5.0"),sQuery(id+"F0.wireOp",EDGE,"E3.6.5.0"),sQuery(id+"F0.wireOp",EDGE,"E3.9.5.0")])],"isStart":false})});
            var Q6;
            Q6=makeQuery(id+"F2.boolean.opBoolean","COPY",FACE,{"derivedFrom":makeQuery(id+"F2.opExtrude","CAP_FACE",FACE,{"disambiguationData":[OSD([sQuery(id+"F0.wireOp",EDGE,"E3.0.6.0"),sQuery(id+"F0.wireOp",EDGE,"E3.3.6.0"),sQuery(id+"F0.wireOp",EDGE,"E3.6.6.0"),sQuery(id+"F0.wireOp",EDGE,"E3.9.6.0")])],"isStart":false})});
            var Q7;
            Q7=makeQuery(id+"F2.boolean.opBoolean","COPY",FACE,{"derivedFrom":makeQuery(id+"F2.opExtrude","CAP_FACE",FACE,{"disambiguationData":[OSD([sQuery(id+"F0.wireOp",EDGE,"E3.0.7.0"),sQuery(id+"F0.wireOp",EDGE,"E3.3.7.0"),sQuery(id+"F0.wireOp",EDGE,"E3.6.7.0"),sQuery(id+"F0.wireOp",EDGE,"E3.9.7.0")])],"isStart":false})});
            var Q8;
            Q8=makeQuery(id+"F2.boolean.opBoolean","COPY",FACE,{"derivedFrom":makeQuery(id+"F2.opExtrude","CAP_FACE",FACE,{"disambiguationData":[OSD([sQuery(id+"F0.wireOp",EDGE,"E9.0.9.0"),sQuery(id+"F0.wireOp",EDGE,"E9.3.9.0"),sQuery(id+"F0.wireOp",EDGE,"E9.6.9.0"),sQuery(id+"F0.wireOp",EDGE,"E9.9.9.0")])],"isStart":false})});
            var Q9;
            Q9=makeQuery(id+"F2.boolean.opBoolean","COPY",FACE,{"derivedFrom":makeQuery(id+"F2.opExtrude","CAP_FACE",FACE,{"disambiguationData":[OSD([sQuery(id+"F0.wireOp",EDGE,"E9.0.8.0"),sQuery(id+"F0.wireOp",EDGE,"E9.3.8.0"),sQuery(id+"F0.wireOp",EDGE,"E9.6.8.0"),sQuery(id+"F0.wireOp",EDGE,"E9.9.8.0")])],"isStart":false})});
            var Q10;
            Q10=makeQuery(id+"F2.boolean.opBoolean","COPY",FACE,{"derivedFrom":makeQuery(id+"F2.opExtrude","CAP_FACE",FACE,{"disambiguationData":[OSD([sQuery(id+"F0.wireOp",EDGE,"E5.7.0.0"),sQuery(id+"F0.wireOp",EDGE,"E5.7.0.1"),sQuery(id+"F0.wireOp",EDGE,"E5.7.0.2"),sQuery(id+"F0.wireOp",EDGE,"E5.7.0.3")])],"isStart":false})});
            var Q11;
            Q11=makeQuery(id+"F2.boolean.opBoolean","COPY",FACE,{"derivedFrom":makeQuery(id+"F2.opExtrude","CAP_FACE",FACE,{"disambiguationData":[OSD([sQuery(id+"F0.wireOp",EDGE,"E5.6.0.0"),sQuery(id+"F0.wireOp",EDGE,"E5.6.0.1"),sQuery(id+"F0.wireOp",EDGE,"E5.6.0.2"),sQuery(id+"F0.wireOp",EDGE,"E5.6.0.3")])],"isStart":false})});
            var Q12;
            Q12=makeQuery(id+"F2.boolean.opBoolean","COPY",FACE,{"derivedFrom":makeQuery(id+"F2.opExtrude","CAP_FACE",FACE,{"disambiguationData":[OSD([sQuery(id+"F0.wireOp",EDGE,"E5.5.0.0"),sQuery(id+"F0.wireOp",EDGE,"E5.5.0.1"),sQuery(id+"F0.wireOp",EDGE,"E5.5.0.2"),sQuery(id+"F0.wireOp",EDGE,"E5.5.0.3")])],"isStart":false})});
            var Q13;
            Q13=makeQuery(id+"F2.boolean.opBoolean","COPY",FACE,{"derivedFrom":makeQuery(id+"F2.opExtrude","CAP_FACE",FACE,{"disambiguationData":[OSD([sQuery(id+"F0.wireOp",EDGE,"E5.4.0.0"),sQuery(id+"F0.wireOp",EDGE,"E5.4.0.1"),sQuery(id+"F0.wireOp",EDGE,"E5.4.0.2"),sQuery(id+"F0.wireOp",EDGE,"E5.4.0.3")])],"isStart":false})});
            var Q14;
            Q14=makeQuery(id+"F2.boolean.opBoolean","COPY",FACE,{"derivedFrom":makeQuery(id+"F2.opExtrude","CAP_FACE",FACE,{"disambiguationData":[OSD([sQuery(id+"F0.wireOp",EDGE,"E5.3.0.0"),sQuery(id+"F0.wireOp",EDGE,"E5.3.0.1"),sQuery(id+"F0.wireOp",EDGE,"E5.3.0.2"),sQuery(id+"F0.wireOp",EDGE,"E5.3.0.3")])],"isStart":false})});
            var Q15;
            Q15=makeQuery(id+"F2.boolean.opBoolean","COPY",FACE,{"derivedFrom":makeQuery(id+"F2.opExtrude","CAP_FACE",FACE,{"disambiguationData":[OSD([sQuery(id+"F0.wireOp",EDGE,"E5.2.0.0"),sQuery(id+"F0.wireOp",EDGE,"E5.2.0.1"),sQuery(id+"F0.wireOp",EDGE,"E5.2.0.2"),sQuery(id+"F0.wireOp",EDGE,"E5.2.0.3")])],"isStart":false})});
            var Q16;
            Q16=makeQuery(id+"F2.boolean.opBoolean","COPY",FACE,{"derivedFrom":makeQuery(id+"F2.opExtrude","CAP_FACE",FACE,{"disambiguationData":[OSD([sQuery(id+"F0.wireOp",EDGE,"E5.1.0.0"),sQuery(id+"F0.wireOp",EDGE,"E5.1.0.1"),sQuery(id+"F0.wireOp",EDGE,"E5.1.0.2"),sQuery(id+"F0.wireOp",EDGE,"E5.1.0.3")])],"isStart":false})});
            var Q17;
            Q17=makeQuery(id+"F2.boolean.opBoolean","COPY",FACE,{"derivedFrom":makeQuery(id+"F2.opExtrude","CAP_FACE",FACE,{"disambiguationData":[OSD([sQuery(id+"F0.wireOp",EDGE,"E4.bottom"),sQuery(id+"F0.wireOp",EDGE,"E4.top"),sQuery(id+"F0.wireOp",EDGE,"E4.left"),sQuery(id+"F0.wireOp",EDGE,"E4.right")])],"isStart":false})});
            var Q18;
            Q18=makeQuery(id+"F2.boolean.opBoolean","COPY",FACE,{"derivedFrom":makeQuery(id+"F2.opExtrude","CAP_FACE",FACE,{"disambiguationData":[OSD([sQuery(id+"F0.wireOp",EDGE,"E6.bottom"),sQuery(id+"F0.wireOp",EDGE,"E6.top"),sQuery(id+"F0.wireOp",EDGE,"E6.left"),sQuery(id+"F0.wireOp",EDGE,"E6.right")])],"isStart":false})});
            var Q19;
            Q19=makeQuery(id+"F2.boolean.opBoolean","COPY",FACE,{"derivedFrom":makeQuery(id+"F2.opExtrude","CAP_FACE",FACE,{"disambiguationData":[OSD([sQuery(id+"F0.wireOp",EDGE,"E7.1.0.0"),sQuery(id+"F0.wireOp",EDGE,"E7.1.0.1"),sQuery(id+"F0.wireOp",EDGE,"E7.1.0.2"),sQuery(id+"F0.wireOp",EDGE,"E7.1.0.3")])],"isStart":false})});
            var Q20;
            Q20=makeQuery(id+"F2.boolean.opBoolean","COPY",FACE,{"derivedFrom":makeQuery(id+"F2.opExtrude","CAP_FACE",FACE,{"disambiguationData":[OSD([sQuery(id+"F0.wireOp",EDGE,"E7.2.0.0"),sQuery(id+"F0.wireOp",EDGE,"E7.2.0.1"),sQuery(id+"F0.wireOp",EDGE,"E7.2.0.2"),sQuery(id+"F0.wireOp",EDGE,"E7.2.0.3")])],"isStart":false})});
            var Q21;
            Q21=makeQuery(id+"F2.boolean.opBoolean","COPY",FACE,{"derivedFrom":makeQuery(id+"F2.opExtrude","CAP_FACE",FACE,{"disambiguationData":[OSD([sQuery(id+"F0.wireOp",EDGE,"E7.3.0.0"),sQuery(id+"F0.wireOp",EDGE,"E7.3.0.1"),sQuery(id+"F0.wireOp",EDGE,"E7.3.0.2"),sQuery(id+"F0.wireOp",EDGE,"E7.3.0.3")])],"isStart":false})});
            var Q22;
            Q22=makeQuery(id+"F2.boolean.opBoolean","COPY",FACE,{"derivedFrom":makeQuery(id+"F2.opExtrude","CAP_FACE",FACE,{"disambiguationData":[OSD([sQuery(id+"F0.wireOp",EDGE,"E7.4.0.0"),sQuery(id+"F0.wireOp",EDGE,"E7.4.0.1"),sQuery(id+"F0.wireOp",EDGE,"E7.4.0.2"),sQuery(id+"F0.wireOp",EDGE,"E7.4.0.3")])],"isStart":false})});
            var Q23;
            Q23=makeQuery(id+"F2.boolean.opBoolean","COPY",FACE,{"derivedFrom":makeQuery(id+"F2.opExtrude","CAP_FACE",FACE,{"disambiguationData":[OSD([sQuery(id+"F0.wireOp",EDGE,"E7.5.0.0"),sQuery(id+"F0.wireOp",EDGE,"E7.5.0.1"),sQuery(id+"F0.wireOp",EDGE,"E7.5.0.2"),sQuery(id+"F0.wireOp",EDGE,"E7.5.0.3")])],"isStart":false})});
            var Q24;
            Q24=makeQuery(id+"F2.boolean.opBoolean","COPY",FACE,{"derivedFrom":makeQuery(id+"F2.opExtrude","CAP_FACE",FACE,{"disambiguationData":[OSD([sQuery(id+"F0.wireOp",EDGE,"E7.6.0.0"),sQuery(id+"F0.wireOp",EDGE,"E7.6.0.1"),sQuery(id+"F0.wireOp",EDGE,"E7.6.0.2"),sQuery(id+"F0.wireOp",EDGE,"E7.6.0.3")])],"isStart":false})});
            var Q25;
            Q25=makeQuery(id+"F2.boolean.opBoolean","COPY",FACE,{"derivedFrom":makeQuery(id+"F2.opExtrude","CAP_FACE",FACE,{"disambiguationData":[OSD([sQuery(id+"F0.wireOp",EDGE,"E7.7.0.0"),sQuery(id+"F0.wireOp",EDGE,"E7.7.0.1"),sQuery(id+"F0.wireOp",EDGE,"E7.7.0.2"),sQuery(id+"F0.wireOp",EDGE,"E7.7.0.3")])],"isStart":false})});
            var Q26;
            Q26=makeQuery(id+"F2.boolean.opBoolean","COPY",FACE,{"derivedFrom":makeQuery(id+"F2.opExtrude","CAP_FACE",FACE,{"disambiguationData":[OSD([sQuery(id+"F0.wireOp",EDGE,"E10.0.8.0"),sQuery(id+"F0.wireOp",EDGE,"E10.3.8.0"),sQuery(id+"F0.wireOp",EDGE,"E10.6.8.0"),sQuery(id+"F0.wireOp",EDGE,"E10.9.8.0")])],"isStart":false})});
            var Q27;
            Q27=makeQuery(id+"F2.boolean.opBoolean","COPY",FACE,{"derivedFrom":makeQuery(id+"F2.opExtrude","CAP_FACE",FACE,{"disambiguationData":[OSD([sQuery(id+"F0.wireOp",EDGE,"E10.0.9.0"),sQuery(id+"F0.wireOp",EDGE,"E10.3.9.0"),sQuery(id+"F0.wireOp",EDGE,"E10.6.9.0"),sQuery(id+"F0.wireOp",EDGE,"E10.9.9.0")])],"isStart":false})});
            var Q28;
            Q28=makeQuery(id+"F2.boolean.opBoolean","COPY",FACE,{"derivedFrom":makeQuery(id+"F2.opExtrude","CAP_FACE",FACE,{"disambiguationData":[OSD([sQuery(id+"F0.wireOp",EDGE,"E10.0.10.0"),sQuery(id+"F0.wireOp",EDGE,"E10.3.10.0"),sQuery(id+"F0.wireOp",EDGE,"E10.6.10.0"),sQuery(id+"F0.wireOp",EDGE,"E10.9.10.0")])],"isStart":false})});
            fillet(context, id + "F6", {"entities" : qUnion([Q0, Q1, Q2, Q3, Q4, Q5, Q6, Q7, Q8, Q9, Q10, Q11, Q12, Q13, Q14, Q15, Q16, Q17, Q18, Q19, Q20, Q21, Q22, Q23, Q24, Q25, Q26, Q27, Q28]), "radius" : 2.54 * mm, "tangentPropagation" : true, "allowEdgeOverflow" : false});
        }
        {
            var Q0;
            Q0=makeQuery(id+"F1.opExtrude","SWEPT_EDGE",EDGE,{"disambiguationData":[OSD([sQuery(id+"F0.wireOp",EDGE,"E0.top"),sQuery(id+"F0.wireOp",EDGE,"E0.left")])]});
            var Q1;
            Q1=makeQuery(id+"F1.opExtrude","SWEPT_EDGE",EDGE,{"disambiguationData":[OSD([sQuery(id+"F0.wireOp",EDGE,"E0.top"),sQuery(id+"F0.wireOp",EDGE,"E0.right")])]});
            var Q2;
            Q2=makeQuery(id+"F1.opExtrude","SWEPT_EDGE",EDGE,{"disambiguationData":[OSD([sQuery(id+"F0.wireOp",EDGE,"E0.bottom"),sQuery(id+"F0.wireOp",EDGE,"E0.right")])]});
            var Q3;
            Q3=makeQuery(id+"F1.opExtrude","SWEPT_EDGE",EDGE,{"disambiguationData":[OSD([sQuery(id+"F0.wireOp",EDGE,"E0.bottom"),sQuery(id+"F0.wireOp",EDGE,"E0.left")])]});
            fillet(context, id + "F7", {"entities" : qUnion([Q0, Q1, Q2, Q3]), "radius" : 5.08 * mm, "tangentPropagation" : true, "allowEdgeOverflow" : false});
        }
    });
